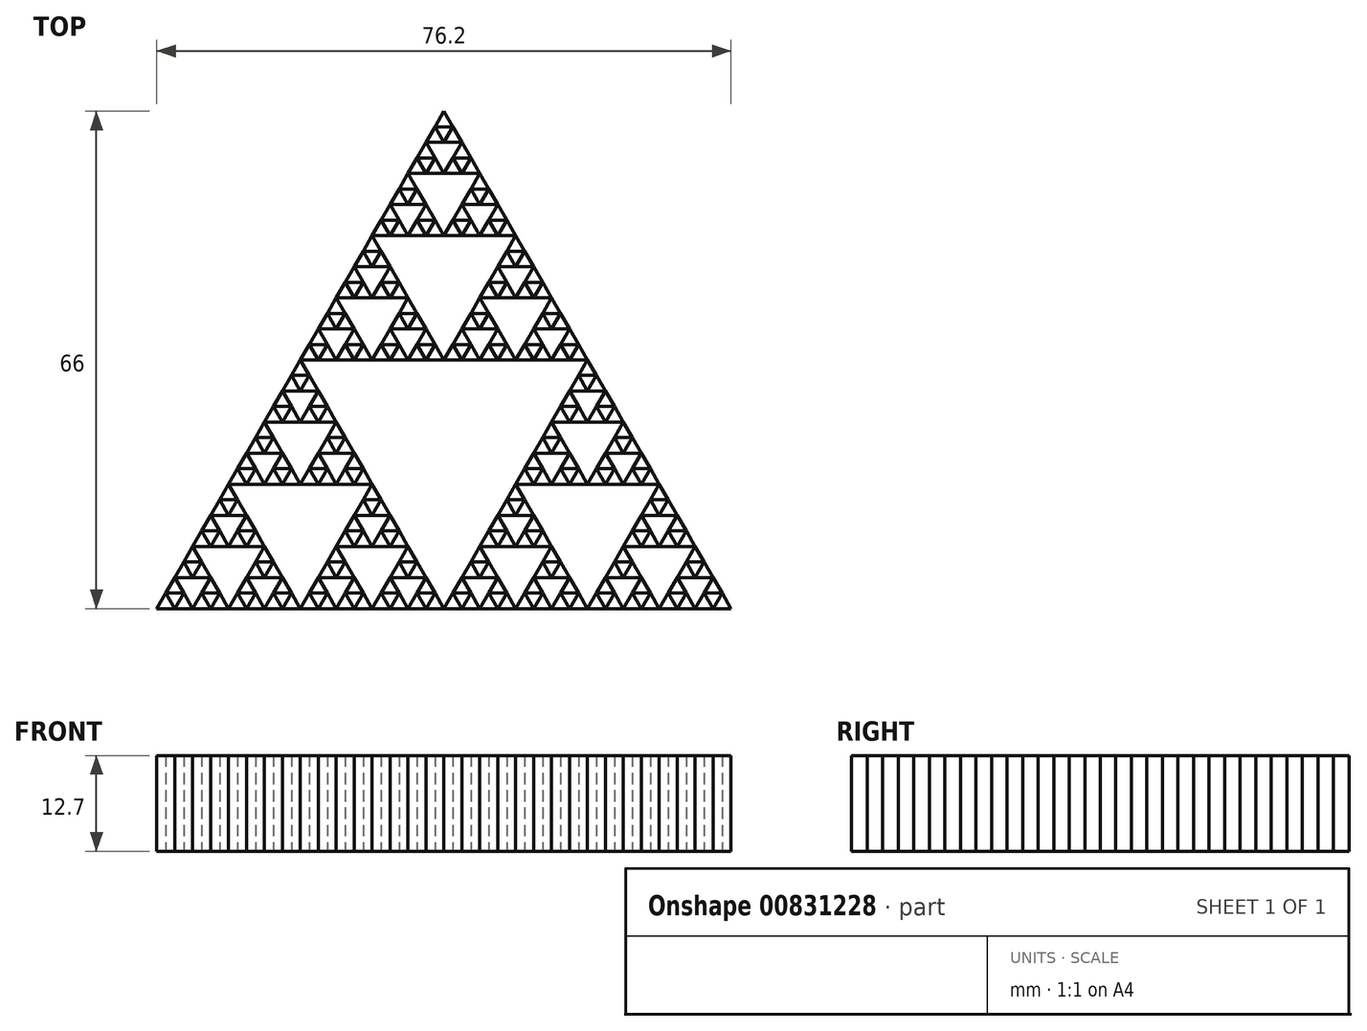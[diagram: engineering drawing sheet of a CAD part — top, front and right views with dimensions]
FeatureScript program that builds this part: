
annotation { "Feature Type Name" : "Feature", "Feature Type Description" : "" }
export const myFeature = defineFeature(function(context is Context, id is Id, definition is map)
    precondition{}
    {
        {
            var Q0;
            Q0=qCreatedBy(makeId("Top.planeOp"),FACE);
            var sketch = newSketch(context, id + "F0", { "sketchPlane" : qUnion([Q0])});
            skLineSegment(sketch, "E0", {"start": v(262.33, 166.64) * mm, "end": v(224.23, 100.64) * mm});
            skLineSegment(sketch, "E1", {"start": v(243.28, 133.64) * mm, "end": v(262.33, 100.64) * mm});
            skLineSegment(sketch, "E2", {"start": v(262.33, 100.64) * mm, "end": v(281.38, 133.64) * mm});
            skLineSegment(sketch, "E3", {"start": v(281.38, 133.64) * mm, "end": v(243.28, 133.64) * mm});
            skLineSegment(sketch, "E4", {"start": v(243.28, 133.64) * mm, "end": v(224.23, 100.64) * mm});
            skLineSegment(sketch, "E5", {"start": v(233.75, 117.14) * mm, "end": v(243.28, 100.64) * mm});
            skLineSegment(sketch, "E6", {"start": v(243.28, 100.64) * mm, "end": v(252.8, 117.14) * mm});
            skLineSegment(sketch, "E7", {"start": v(233.75, 117.14) * mm, "end": v(252.8, 117.14) * mm});
            skLineSegment(sketch, "E8", {"start": v(252.8, 150.14) * mm, "end": v(262.33, 133.64) * mm});
            skLineSegment(sketch, "E9", {"start": v(262.33, 133.64) * mm, "end": v(271.85, 150.14) * mm});
            skLineSegment(sketch, "E10", {"start": v(271.85, 150.14) * mm, "end": v(252.8, 150.14) * mm});
            skLineSegment(sketch, "E11", {"start": v(243.28, 117.14) * mm, "end": v(238.51, 125.4) * mm});
            skLineSegment(sketch, "E12", {"start": v(238.51, 125.4) * mm, "end": v(248.04, 125.4) * mm});
            skLineSegment(sketch, "E13", {"start": v(248.04, 125.4) * mm, "end": v(243.28, 117.14) * mm});
            skLineSegment(sketch, "E14", {"start": v(233.75, 100.64) * mm, "end": v(238.51, 108.9) * mm});
            skLineSegment(sketch, "E15", {"start": v(238.51, 108.9) * mm, "end": v(228.99, 108.9) * mm});
            skLineSegment(sketch, "E16", {"start": v(228.99, 108.9) * mm, "end": v(233.75, 100.64) * mm});
            skLineSegment(sketch, "E17", {"start": v(248.04, 108.9) * mm, "end": v(257.56, 108.9) * mm});
            skLineSegment(sketch, "E18", {"start": v(257.56, 108.9) * mm, "end": v(252.8, 100.64) * mm});
            skLineSegment(sketch, "E19", {"start": v(252.8, 100.64) * mm, "end": v(248.04, 108.9) * mm});
            skLineSegment(sketch, "E20", {"start": v(271.85, 117.14) * mm, "end": v(281.38, 100.64) * mm});
            skLineSegment(sketch, "E21", {"start": v(281.38, 100.64) * mm, "end": v(290.9, 117.14) * mm});
            skLineSegment(sketch, "E22", {"start": v(290.9, 117.14) * mm, "end": v(271.85, 117.14) * mm});
            skLineSegment(sketch, "E23", {"start": v(276.61, 108.9) * mm, "end": v(267.09, 108.9) * mm});
            skLineSegment(sketch, "E24", {"start": v(267.09, 108.9) * mm, "end": v(271.85, 100.64) * mm});
            skLineSegment(sketch, "E25", {"start": v(271.85, 100.64) * mm, "end": v(276.61, 108.9) * mm});
            skLineSegment(sketch, "E26", {"start": v(286.14, 108.9) * mm, "end": v(295.66, 108.9) * mm});
            skLineSegment(sketch, "E27", {"start": v(295.66, 108.9) * mm, "end": v(290.9, 100.64) * mm});
            skLineSegment(sketch, "E28", {"start": v(290.9, 100.64) * mm, "end": v(286.14, 108.9) * mm});
            skLineSegment(sketch, "E29", {"start": v(281.38, 117.14) * mm, "end": v(286.14, 125.4) * mm});
            skLineSegment(sketch, "E30", {"start": v(286.14, 125.4) * mm, "end": v(276.61, 125.4) * mm});
            skLineSegment(sketch, "E31", {"start": v(276.61, 125.4) * mm, "end": v(281.38, 117.14) * mm});
            skLineSegment(sketch, "E32", {"start": v(248.04, 141.89) * mm, "end": v(252.8, 133.64) * mm});
            skPoint(sketch, "E32.startSnap0", {"position": v(267.09, 141.89) * mm});
            skLineSegment(sketch, "E33", {"start": v(252.8, 133.64) * mm, "end": v(257.56, 141.89) * mm});
            skLineSegment(sketch, "E34", {"start": v(257.56, 141.89) * mm, "end": v(248.04, 141.89) * mm});
            skLineSegment(sketch, "E35", {"start": v(267.09, 141.89) * mm, "end": v(276.61, 141.89) * mm});
            skLineSegment(sketch, "E36", {"start": v(276.61, 141.89) * mm, "end": v(271.85, 133.64) * mm});
            skLineSegment(sketch, "E37", {"start": v(271.85, 133.64) * mm, "end": v(267.09, 141.89) * mm});
            skLineSegment(sketch, "E38", {"start": v(262.33, 150.14) * mm, "end": v(257.56, 158.39) * mm});
            skLineSegment(sketch, "E39", {"start": v(257.56, 158.39) * mm, "end": v(267.09, 158.39) * mm});
            skLineSegment(sketch, "E40", {"start": v(267.09, 158.39) * mm, "end": v(262.33, 150.14) * mm});
            skLineSegment(sketch, "E41", {"start": v(238.51, 117.14) * mm, "end": v(240.9, 121.27) * mm});
            skLineSegment(sketch, "E42", {"start": v(240.9, 121.27) * mm, "end": v(236.13, 121.27) * mm});
            skLineSegment(sketch, "E43", {"start": v(236.13, 121.27) * mm, "end": v(238.51, 117.14) * mm});
            skLineSegment(sketch, "E44", {"start": v(245.66, 121.27) * mm, "end": v(250.42, 121.27) * mm});
            skLineSegment(sketch, "E45", {"start": v(250.42, 121.27) * mm, "end": v(248.04, 117.14) * mm});
            skLineSegment(sketch, "E46", {"start": v(248.04, 117.14) * mm, "end": v(245.66, 121.27) * mm});
            skLineSegment(sketch, "E47", {"start": v(243.28, 125.4) * mm, "end": v(245.66, 129.52) * mm});
            skLineSegment(sketch, "E48", {"start": v(245.66, 129.52) * mm, "end": v(240.9, 129.52) * mm});
            skLineSegment(sketch, "E49", {"start": v(240.9, 129.52) * mm, "end": v(243.28, 125.4) * mm});
            skLineSegment(sketch, "E50", {"start": v(233.75, 108.9) * mm, "end": v(236.13, 113.02) * mm});
            skLineSegment(sketch, "E51", {"start": v(236.13, 113.02) * mm, "end": v(231.37, 113.02) * mm});
            skLineSegment(sketch, "E52", {"start": v(231.37, 113.02) * mm, "end": v(233.75, 108.9) * mm});
            skLineSegment(sketch, "E53", {"start": v(228.99, 100.64) * mm, "end": v(231.37, 104.77) * mm});
            skLineSegment(sketch, "E54", {"start": v(231.37, 104.77) * mm, "end": v(226.6, 104.77) * mm});
            skLineSegment(sketch, "E55", {"start": v(226.6, 104.77) * mm, "end": v(228.99, 100.64) * mm});
            skLineSegment(sketch, "E56", {"start": v(236.13, 104.77) * mm, "end": v(238.51, 100.64) * mm});
            skLineSegment(sketch, "E57", {"start": v(238.51, 100.64) * mm, "end": v(240.9, 104.77) * mm});
            skLineSegment(sketch, "E58", {"start": v(240.9, 104.77) * mm, "end": v(236.13, 104.77) * mm});
            skLineSegment(sketch, "E59", {"start": v(245.66, 104.77) * mm, "end": v(248.04, 100.64) * mm});
            skLineSegment(sketch, "E60", {"start": v(248.04, 100.64) * mm, "end": v(250.42, 104.77) * mm});
            skLineSegment(sketch, "E61", {"start": v(250.42, 104.77) * mm, "end": v(245.66, 104.77) * mm});
            skLineSegment(sketch, "E62", {"start": v(255.18, 104.77) * mm, "end": v(259.95, 104.77) * mm});
            skLineSegment(sketch, "E63", {"start": v(259.95, 104.77) * mm, "end": v(257.56, 100.64) * mm});
            skLineSegment(sketch, "E64", {"start": v(255.18, 104.77) * mm, "end": v(257.56, 100.64) * mm});
            skLineSegment(sketch, "E65", {"start": v(252.8, 108.9) * mm, "end": v(255.18, 113.02) * mm});
            skLineSegment(sketch, "E66", {"start": v(255.18, 113.02) * mm, "end": v(250.42, 113.02) * mm});
            skLineSegment(sketch, "E67", {"start": v(250.42, 113.02) * mm, "end": v(252.8, 108.9) * mm});
            skLineSegment(sketch, "E68", {"start": v(240.9, 100.64) * mm, "end": v(242.09, 102.7) * mm});
            skLineSegment(sketch, "E69", {"start": v(242.09, 102.7) * mm, "end": v(239.7, 102.7) * mm});
            skLineSegment(sketch, "E70", {"start": v(239.7, 102.7) * mm, "end": v(240.9, 100.64) * mm});
            skLineSegment(sketch, "E71", {"start": v(238.51, 100.64) * mm, "end": v(233.75, 100.64) * mm});
            skLineSegment(sketch, "E72", {"start": v(236.13, 100.64) * mm, "end": v(237.32, 102.7) * mm});
            skLineSegment(sketch, "E73", {"start": v(237.32, 102.7) * mm, "end": v(234.94, 102.7) * mm});
            skLineSegment(sketch, "E74", {"start": v(234.94, 102.7) * mm, "end": v(236.13, 100.64) * mm});
            skLineSegment(sketch, "E75", {"start": v(228.99, 100.64) * mm, "end": v(233.75, 100.64) * mm});
            skLineSegment(sketch, "E76", {"start": v(231.37, 100.64) * mm, "end": v(232.56, 102.7) * mm});
            skLineSegment(sketch, "E77", {"start": v(232.56, 102.7) * mm, "end": v(230.18, 102.7) * mm});
            skLineSegment(sketch, "E78", {"start": v(230.18, 102.7) * mm, "end": v(231.37, 100.64) * mm});
            skLineSegment(sketch, "E79", {"start": v(227.8, 102.7) * mm, "end": v(226.6, 100.64) * mm});
            skLineSegment(sketch, "E80", {"start": v(226.6, 100.64) * mm, "end": v(225.42, 102.7) * mm});
            skLineSegment(sketch, "E81", {"start": v(225.42, 102.7) * mm, "end": v(227.8, 102.7) * mm});
            skLineSegment(sketch, "E82", {"start": v(228.99, 104.77) * mm, "end": v(227.8, 106.83) * mm});
            skLineSegment(sketch, "E83", {"start": v(227.8, 106.83) * mm, "end": v(230.18, 106.83) * mm});
            skLineSegment(sketch, "E84", {"start": v(230.18, 106.83) * mm, "end": v(228.99, 104.77) * mm});
            skLineSegment(sketch, "E85", {"start": v(238.51, 104.77) * mm, "end": v(239.7, 106.83) * mm});
            skLineSegment(sketch, "E86", {"start": v(239.7, 106.83) * mm, "end": v(237.32, 106.83) * mm});
            skLineSegment(sketch, "E87", {"start": v(237.32, 106.83) * mm, "end": v(238.51, 104.77) * mm});
            skLineSegment(sketch, "E88", {"start": v(234.94, 110.96) * mm, "end": v(237.32, 110.96) * mm});
            skLineSegment(sketch, "E89", {"start": v(237.32, 110.96) * mm, "end": v(236.13, 108.9) * mm});
            skLineSegment(sketch, "E90", {"start": v(236.13, 108.9) * mm, "end": v(234.94, 110.96) * mm});
            skLineSegment(sketch, "E91", {"start": v(232.56, 110.96) * mm, "end": v(230.18, 110.96) * mm});
            skLineSegment(sketch, "E92", {"start": v(230.18, 110.96) * mm, "end": v(231.37, 108.9) * mm});
            skLineSegment(sketch, "E93", {"start": v(231.37, 108.9) * mm, "end": v(232.56, 110.96) * mm});
            skLineSegment(sketch, "E94", {"start": v(233.75, 117.14) * mm, "end": v(231.37, 113.02) * mm});
            skLineSegment(sketch, "E95", {"start": v(232.56, 115.08) * mm, "end": v(233.75, 113.02) * mm});
            skLineSegment(sketch, "E96", {"start": v(233.75, 113.02) * mm, "end": v(234.94, 115.08) * mm});
            skLineSegment(sketch, "E97", {"start": v(234.94, 115.08) * mm, "end": v(232.56, 115.08) * mm});
            skLineSegment(sketch, "E98", {"start": v(246.85, 102.7) * mm, "end": v(244.47, 102.7) * mm});
            skLineSegment(sketch, "E99", {"start": v(244.47, 102.7) * mm, "end": v(245.66, 100.64) * mm});
            skLineSegment(sketch, "E100", {"start": v(245.66, 100.64) * mm, "end": v(246.85, 102.7) * mm});
            skLineSegment(sketch, "E101", {"start": v(249.23, 102.7) * mm, "end": v(251.61, 102.7) * mm});
            skLineSegment(sketch, "E102", {"start": v(251.61, 102.7) * mm, "end": v(250.42, 100.64) * mm});
            skLineSegment(sketch, "E103", {"start": v(250.42, 100.64) * mm, "end": v(249.23, 102.7) * mm});
            skLineSegment(sketch, "E104", {"start": v(248.04, 104.77) * mm, "end": v(249.23, 106.83) * mm});
            skLineSegment(sketch, "E105", {"start": v(249.23, 106.83) * mm, "end": v(246.85, 106.83) * mm});
            skLineSegment(sketch, "E106", {"start": v(246.85, 106.83) * mm, "end": v(248.04, 104.77) * mm});
            skLineSegment(sketch, "E107", {"start": v(257.56, 104.77) * mm, "end": v(258.76, 106.83) * mm});
            skLineSegment(sketch, "E108", {"start": v(258.76, 106.83) * mm, "end": v(256.37, 106.83) * mm});
            skLineSegment(sketch, "E109", {"start": v(256.37, 106.83) * mm, "end": v(257.56, 104.77) * mm});
            skLineSegment(sketch, "E110", {"start": v(256.37, 102.7) * mm, "end": v(254, 102.7) * mm});
            skLineSegment(sketch, "E111", {"start": v(254, 102.7) * mm, "end": v(255.18, 100.64) * mm});
            skLineSegment(sketch, "E112", {"start": v(255.18, 100.64) * mm, "end": v(256.37, 102.7) * mm});
            skLineSegment(sketch, "E113", {"start": v(258.76, 102.7) * mm, "end": v(259.95, 100.64) * mm});
            skLineSegment(sketch, "E114", {"start": v(259.95, 100.64) * mm, "end": v(261.14, 102.7) * mm});
            skLineSegment(sketch, "E115", {"start": v(261.14, 102.7) * mm, "end": v(258.76, 102.7) * mm});
            skLineSegment(sketch, "E116", {"start": v(251.61, 110.96) * mm, "end": v(250.42, 108.9) * mm});
            skLineSegment(sketch, "E117", {"start": v(250.42, 108.9) * mm, "end": v(249.23, 110.96) * mm});
            skLineSegment(sketch, "E118", {"start": v(249.23, 110.96) * mm, "end": v(251.61, 110.96) * mm});
            skLineSegment(sketch, "E119", {"start": v(254, 110.96) * mm, "end": v(256.37, 110.96) * mm});
            skLineSegment(sketch, "E120", {"start": v(256.37, 110.96) * mm, "end": v(255.18, 108.9) * mm});
            skLineSegment(sketch, "E121", {"start": v(255.18, 108.9) * mm, "end": v(254, 110.96) * mm});
            skLineSegment(sketch, "E122", {"start": v(252.8, 113.02) * mm, "end": v(254, 115.08) * mm});
            skLineSegment(sketch, "E123", {"start": v(254, 115.08) * mm, "end": v(251.61, 115.08) * mm});
            skLineSegment(sketch, "E124", {"start": v(251.61, 115.08) * mm, "end": v(252.8, 113.02) * mm});
            skLineSegment(sketch, "E125", {"start": v(239.7, 119.2) * mm, "end": v(242.09, 119.2) * mm});
            skLineSegment(sketch, "E126", {"start": v(242.09, 119.2) * mm, "end": v(240.9, 117.14) * mm});
            skLineSegment(sketch, "E127", {"start": v(240.9, 117.14) * mm, "end": v(239.7, 119.2) * mm});
            skLineSegment(sketch, "E128", {"start": v(237.32, 119.2) * mm, "end": v(234.94, 119.2) * mm});
            skLineSegment(sketch, "E129", {"start": v(234.94, 119.2) * mm, "end": v(236.13, 117.14) * mm});
            skLineSegment(sketch, "E130", {"start": v(236.13, 117.14) * mm, "end": v(237.32, 119.2) * mm});
            skLineSegment(sketch, "E131", {"start": v(238.51, 121.27) * mm, "end": v(237.32, 123.33) * mm});
            skLineSegment(sketch, "E132", {"start": v(237.32, 123.33) * mm, "end": v(239.7, 123.33) * mm});
            skLineSegment(sketch, "E133", {"start": v(239.7, 123.33) * mm, "end": v(238.51, 121.27) * mm});
            skLineSegment(sketch, "E134", {"start": v(242.09, 127.45) * mm, "end": v(240.9, 125.4) * mm});
            skLineSegment(sketch, "E135", {"start": v(240.9, 125.4) * mm, "end": v(239.7, 127.45) * mm});
            skLineSegment(sketch, "E136", {"start": v(239.7, 127.45) * mm, "end": v(242.09, 127.45) * mm});
            skLineSegment(sketch, "E137", {"start": v(244.47, 127.45) * mm, "end": v(246.85, 127.45) * mm});
            skLineSegment(sketch, "E138", {"start": v(246.85, 127.45) * mm, "end": v(245.66, 125.4) * mm});
            skLineSegment(sketch, "E139", {"start": v(245.66, 125.4) * mm, "end": v(244.47, 127.45) * mm});
            skLineSegment(sketch, "E140", {"start": v(243.28, 129.52) * mm, "end": v(244.47, 131.58) * mm});
            skLineSegment(sketch, "E141", {"start": v(244.47, 131.58) * mm, "end": v(242.09, 131.58) * mm});
            skLineSegment(sketch, "E142", {"start": v(242.09, 131.58) * mm, "end": v(243.28, 129.52) * mm});
            skLineSegment(sketch, "E143", {"start": v(246.85, 119.2) * mm, "end": v(244.47, 119.2) * mm});
            skLineSegment(sketch, "E144", {"start": v(244.47, 119.2) * mm, "end": v(245.66, 117.14) * mm});
            skLineSegment(sketch, "E145", {"start": v(245.66, 117.14) * mm, "end": v(246.85, 119.2) * mm});
            skLineSegment(sketch, "E146", {"start": v(246.85, 123.33) * mm, "end": v(249.23, 123.33) * mm});
            skLineSegment(sketch, "E147", {"start": v(249.23, 123.33) * mm, "end": v(248.04, 121.27) * mm});
            skLineSegment(sketch, "E148", {"start": v(248.04, 121.27) * mm, "end": v(246.85, 123.33) * mm});
            skLineSegment(sketch, "E149", {"start": v(249.23, 119.2) * mm, "end": v(251.61, 119.2) * mm});
            skLineSegment(sketch, "E150", {"start": v(251.61, 119.2) * mm, "end": v(250.42, 117.14) * mm});
            skLineSegment(sketch, "E151", {"start": v(250.42, 117.14) * mm, "end": v(249.23, 119.2) * mm});
            skLineSegment(sketch, "E152.MirrorCS", {"start": v(298.05, 100.64) * mm, "end": v(299.24, 102.7) * mm});
            skLineSegment(sketch, "E153.MirrorCS", {"start": v(299.24, 102.7) * mm, "end": v(296.86, 102.7) * mm});
            skLineSegment(sketch, "E154.MirrorCS", {"start": v(296.86, 102.7) * mm, "end": v(298.05, 100.64) * mm});
            skLineSegment(sketch, "E155.MirrorCS", {"start": v(298.05, 104.77) * mm, "end": v(295.66, 100.64) * mm});
            skLineSegment(sketch, "E156.MirrorCS", {"start": v(295.66, 100.64) * mm, "end": v(293.28, 104.77) * mm});
            skLineSegment(sketch, "E157.MirrorCS", {"start": v(289.71, 102.7) * mm, "end": v(288.52, 100.64) * mm});
            skLineSegment(sketch, "E158.MirrorCS", {"start": v(288.52, 100.64) * mm, "end": v(287.33, 102.7) * mm});
            skLineSegment(sketch, "E159.MirrorCS", {"start": v(287.33, 102.7) * mm, "end": v(289.71, 102.7) * mm});
            skLineSegment(sketch, "E160.MirrorCS", {"start": v(293.28, 104.77) * mm, "end": v(298.05, 104.77) * mm});
            skLineSegment(sketch, "E161.MirrorCS", {"start": v(294.47, 106.83) * mm, "end": v(295.66, 104.77) * mm});
            skLineSegment(sketch, "E162.MirrorCS", {"start": v(295.66, 104.77) * mm, "end": v(296.86, 106.83) * mm});
            skLineSegment(sketch, "E163.MirrorCS", {"start": v(296.86, 106.83) * mm, "end": v(294.47, 106.83) * mm});
            skLineSegment(sketch, "E164.MirrorCS", {"start": v(293.28, 100.64) * mm, "end": v(292.1, 102.7) * mm});
            skLineSegment(sketch, "E165.MirrorCS", {"start": v(292.1, 102.7) * mm, "end": v(294.47, 102.7) * mm});
            skLineSegment(sketch, "E166.MirrorCS", {"start": v(294.47, 102.7) * mm, "end": v(293.28, 100.64) * mm});
            skLineSegment(sketch, "E167.MirrorCS", {"start": v(284.95, 102.7) * mm, "end": v(283.76, 100.64) * mm});
            skLineSegment(sketch, "E168.MirrorCS", {"start": v(283.76, 100.64) * mm, "end": v(282.57, 102.7) * mm});
            skLineSegment(sketch, "E169.MirrorCS", {"start": v(282.57, 102.7) * mm, "end": v(284.95, 102.7) * mm});
            skLineSegment(sketch, "E170.MirrorCS", {"start": v(286.14, 104.77) * mm, "end": v(284.95, 106.83) * mm});
            skLineSegment(sketch, "E171.MirrorCS", {"start": v(287.33, 106.83) * mm, "end": v(286.14, 104.77) * mm});
            skLineSegment(sketch, "E172.MirrorCS", {"start": v(284.95, 106.83) * mm, "end": v(287.33, 106.83) * mm});
            skLineSegment(sketch, "E173.MirrorCS", {"start": v(286.14, 100.64) * mm, "end": v(283.76, 104.77) * mm});
            skLineSegment(sketch, "E174.MirrorCS", {"start": v(288.52, 104.77) * mm, "end": v(286.14, 100.64) * mm});
            skLineSegment(sketch, "E175.MirrorCS", {"start": v(283.76, 104.77) * mm, "end": v(288.52, 104.77) * mm});
            skLineSegment(sketch, "E176.MirrorCS", {"start": v(287.33, 110.96) * mm, "end": v(288.52, 108.9) * mm});
            skLineSegment(sketch, "E177.MirrorCS", {"start": v(288.52, 108.9) * mm, "end": v(289.71, 110.96) * mm});
            skLineSegment(sketch, "E178.MirrorCS", {"start": v(289.71, 110.96) * mm, "end": v(287.33, 110.96) * mm});
            skLineSegment(sketch, "E179.MirrorCS", {"start": v(290.9, 108.9) * mm, "end": v(288.52, 113.02) * mm});
            skLineSegment(sketch, "E180.MirrorCS", {"start": v(288.52, 113.02) * mm, "end": v(293.28, 113.02) * mm});
            skLineSegment(sketch, "E181.MirrorCS", {"start": v(290.9, 113.02) * mm, "end": v(289.71, 115.08) * mm});
            skLineSegment(sketch, "E182.MirrorCS", {"start": v(292.1, 115.08) * mm, "end": v(290.9, 113.02) * mm});
            skLineSegment(sketch, "E183.MirrorCS", {"start": v(289.71, 115.08) * mm, "end": v(292.1, 115.08) * mm});
            skLineSegment(sketch, "E184.MirrorCS", {"start": v(293.28, 113.02) * mm, "end": v(290.9, 108.9) * mm});
            skLineSegment(sketch, "E185.MirrorCS", {"start": v(292.1, 110.96) * mm, "end": v(294.47, 110.96) * mm});
            skLineSegment(sketch, "E186.MirrorCS", {"start": v(293.28, 108.9) * mm, "end": v(292.1, 110.96) * mm});
            skLineSegment(sketch, "E187.MirrorCS", {"start": v(294.47, 110.96) * mm, "end": v(293.28, 108.9) * mm});
            skLineSegment(sketch, "E188.MirrorCS", {"start": v(288.52, 117.14) * mm, "end": v(287.33, 119.2) * mm});
            skLineSegment(sketch, "E189.MirrorCS", {"start": v(289.71, 119.2) * mm, "end": v(288.52, 117.14) * mm});
            skLineSegment(sketch, "E190.MirrorCS", {"start": v(287.33, 119.2) * mm, "end": v(289.71, 119.2) * mm});
            skLineSegment(sketch, "E191.MirrorCS", {"start": v(288.52, 121.27) * mm, "end": v(286.14, 117.14) * mm});
            skLineSegment(sketch, "E192.MirrorCS", {"start": v(286.14, 117.14) * mm, "end": v(283.76, 121.27) * mm});
            skLineSegment(sketch, "E193.MirrorCS", {"start": v(284.95, 119.2) * mm, "end": v(282.57, 119.2) * mm});
            skLineSegment(sketch, "E194.MirrorCS", {"start": v(283.76, 117.14) * mm, "end": v(284.95, 119.2) * mm});
            skLineSegment(sketch, "E195.MirrorCS", {"start": v(282.57, 119.2) * mm, "end": v(283.76, 117.14) * mm});
            skLineSegment(sketch, "E196.MirrorCS", {"start": v(283.76, 121.27) * mm, "end": v(288.52, 121.27) * mm});
            skLineSegment(sketch, "E197.MirrorCS", {"start": v(284.95, 123.33) * mm, "end": v(286.14, 121.27) * mm});
            skLineSegment(sketch, "E198.MirrorCS", {"start": v(286.14, 121.27) * mm, "end": v(287.33, 123.33) * mm});
            skLineSegment(sketch, "E199.MirrorCS", {"start": v(287.33, 123.33) * mm, "end": v(284.95, 123.33) * mm});
            skLineSegment(sketch, "E200.MirrorCS", {"start": v(274.23, 117.14) * mm, "end": v(275.42, 119.2) * mm});
            skLineSegment(sketch, "E201.MirrorCS", {"start": v(275.42, 119.2) * mm, "end": v(273.04, 119.2) * mm});
            skLineSegment(sketch, "E202.MirrorCS", {"start": v(273.04, 119.2) * mm, "end": v(274.23, 117.14) * mm});
            skLineSegment(sketch, "E203.MirrorCS", {"start": v(279, 117.14) * mm, "end": v(277.8, 119.2) * mm});
            skLineSegment(sketch, "E204.MirrorCS", {"start": v(280.19, 119.2) * mm, "end": v(279, 117.14) * mm});
            skLineSegment(sketch, "E205.MirrorCS", {"start": v(277.8, 119.2) * mm, "end": v(280.19, 119.2) * mm});
            skLineSegment(sketch, "E206.MirrorCS", {"start": v(279, 121.27) * mm, "end": v(274.23, 121.27) * mm});
            skLineSegment(sketch, "E207.MirrorCS", {"start": v(276.61, 117.14) * mm, "end": v(279, 121.27) * mm});
            skLineSegment(sketch, "E208.MirrorCS", {"start": v(274.23, 121.27) * mm, "end": v(276.61, 117.14) * mm});
            skLineSegment(sketch, "E209.MirrorCS", {"start": v(275.42, 123.33) * mm, "end": v(276.61, 121.27) * mm});
            skLineSegment(sketch, "E210.MirrorCS", {"start": v(277.8, 123.33) * mm, "end": v(275.42, 123.33) * mm});
            skLineSegment(sketch, "E211.MirrorCS", {"start": v(276.61, 121.27) * mm, "end": v(277.8, 123.33) * mm});
            skLineSegment(sketch, "E212.MirrorCS", {"start": v(277.8, 127.45) * mm, "end": v(279, 125.4) * mm});
            skLineSegment(sketch, "E213.MirrorCS", {"start": v(279, 125.4) * mm, "end": v(280.19, 127.45) * mm});
            skLineSegment(sketch, "E214.MirrorCS", {"start": v(281.38, 125.4) * mm, "end": v(279, 129.52) * mm});
            skLineSegment(sketch, "E215.MirrorCS", {"start": v(283.76, 129.52) * mm, "end": v(281.38, 125.4) * mm});
            skLineSegment(sketch, "E216.MirrorCS", {"start": v(282.57, 127.45) * mm, "end": v(283.76, 125.4) * mm});
            skLineSegment(sketch, "E217.MirrorCS", {"start": v(283.76, 125.4) * mm, "end": v(284.95, 127.45) * mm});
            skLineSegment(sketch, "E218.MirrorCS", {"start": v(284.95, 127.45) * mm, "end": v(282.57, 127.45) * mm});
            skLineSegment(sketch, "E219.MirrorCS", {"start": v(280.19, 127.45) * mm, "end": v(277.8, 127.45) * mm});
            skLineSegment(sketch, "E220.MirrorCS", {"start": v(281.38, 129.52) * mm, "end": v(280.19, 131.58) * mm});
            skLineSegment(sketch, "E221.MirrorCS", {"start": v(282.57, 131.58) * mm, "end": v(281.38, 129.52) * mm});
            skLineSegment(sketch, "E222.MirrorCS", {"start": v(280.19, 131.58) * mm, "end": v(282.57, 131.58) * mm});
            skLineSegment(sketch, "E223.MirrorCS", {"start": v(279, 129.52) * mm, "end": v(283.76, 129.52) * mm});
            skLineSegment(sketch, "E224.MirrorCS", {"start": v(265.9, 102.7) * mm, "end": v(264.7, 100.64) * mm});
            skLineSegment(sketch, "E225.MirrorCS", {"start": v(264.7, 100.64) * mm, "end": v(263.52, 102.7) * mm});
            skLineSegment(sketch, "E226.MirrorCS", {"start": v(263.52, 102.7) * mm, "end": v(265.9, 102.7) * mm});
            skLineSegment(sketch, "E227.MirrorCS", {"start": v(264.7, 104.77) * mm, "end": v(267.09, 100.64) * mm});
            skLineSegment(sketch, "E228.MirrorCS", {"start": v(269.47, 104.77) * mm, "end": v(267.09, 100.64) * mm});
            skLineSegment(sketch, "E229.MirrorCS", {"start": v(269.47, 100.64) * mm, "end": v(268.28, 102.7) * mm});
            skLineSegment(sketch, "E230.MirrorCS", {"start": v(270.66, 102.7) * mm, "end": v(269.47, 100.64) * mm});
            skLineSegment(sketch, "E231.MirrorCS", {"start": v(268.28, 102.7) * mm, "end": v(270.66, 102.7) * mm});
            skLineSegment(sketch, "E232.MirrorCS", {"start": v(269.47, 104.77) * mm, "end": v(264.7, 104.77) * mm});
            skLineSegment(sketch, "E233.MirrorCS", {"start": v(268.28, 106.83) * mm, "end": v(267.09, 104.77) * mm});
            skLineSegment(sketch, "E234.MirrorCS", {"start": v(267.09, 104.77) * mm, "end": v(265.9, 106.83) * mm});
            skLineSegment(sketch, "E235.MirrorCS", {"start": v(265.9, 106.83) * mm, "end": v(268.28, 106.83) * mm});
            skLineSegment(sketch, "E236.MirrorCS", {"start": v(273.04, 102.7) * mm, "end": v(274.23, 100.64) * mm});
            skLineSegment(sketch, "E237.MirrorCS", {"start": v(274.23, 100.64) * mm, "end": v(275.42, 102.7) * mm});
            skLineSegment(sketch, "E238.MirrorCS", {"start": v(275.42, 102.7) * mm, "end": v(273.04, 102.7) * mm});
            skLineSegment(sketch, "E239.MirrorCS", {"start": v(276.61, 100.64) * mm, "end": v(274.23, 104.77) * mm});
            skLineSegment(sketch, "E240.MirrorCS", {"start": v(274.23, 104.77) * mm, "end": v(279, 104.77) * mm});
            skLineSegment(sketch, "E241.MirrorCS", {"start": v(276.61, 104.77) * mm, "end": v(275.42, 106.83) * mm});
            skLineSegment(sketch, "E242.MirrorCS", {"start": v(275.42, 106.83) * mm, "end": v(277.8, 106.83) * mm});
            skLineSegment(sketch, "E243.MirrorCS", {"start": v(277.8, 106.83) * mm, "end": v(276.61, 104.77) * mm});
            skLineSegment(sketch, "E244.MirrorCS", {"start": v(279, 104.77) * mm, "end": v(276.61, 100.64) * mm});
            skLineSegment(sketch, "E245.MirrorCS", {"start": v(277.8, 102.7) * mm, "end": v(280.19, 102.7) * mm});
            skLineSegment(sketch, "E246.MirrorCS", {"start": v(279, 100.64) * mm, "end": v(277.8, 102.7) * mm});
            skLineSegment(sketch, "E247.MirrorCS", {"start": v(280.19, 102.7) * mm, "end": v(279, 100.64) * mm});
            skLineSegment(sketch, "E248.MirrorCS", {"start": v(273.04, 110.96) * mm, "end": v(274.23, 108.9) * mm});
            skLineSegment(sketch, "E249.MirrorCS", {"start": v(274.23, 108.9) * mm, "end": v(275.42, 110.96) * mm});
            skLineSegment(sketch, "E250.MirrorCS", {"start": v(275.42, 110.96) * mm, "end": v(273.04, 110.96) * mm});
            skLineSegment(sketch, "E251.MirrorCS", {"start": v(274.23, 113.02) * mm, "end": v(271.85, 108.9) * mm});
            skLineSegment(sketch, "E252.MirrorCS", {"start": v(271.85, 108.9) * mm, "end": v(269.47, 113.02) * mm});
            skLineSegment(sketch, "E253.MirrorCS", {"start": v(270.66, 110.96) * mm, "end": v(268.28, 110.96) * mm});
            skLineSegment(sketch, "E254.MirrorCS", {"start": v(269.47, 108.9) * mm, "end": v(270.66, 110.96) * mm});
            skLineSegment(sketch, "E255.MirrorCS", {"start": v(268.28, 110.96) * mm, "end": v(269.47, 108.9) * mm});
            skLineSegment(sketch, "E256.MirrorCS", {"start": v(271.85, 113.02) * mm, "end": v(270.66, 115.08) * mm});
            skLineSegment(sketch, "E257.MirrorCS", {"start": v(273.04, 115.08) * mm, "end": v(271.85, 113.02) * mm});
            skLineSegment(sketch, "E258.MirrorCS", {"start": v(270.66, 115.08) * mm, "end": v(273.04, 115.08) * mm});
            skLineSegment(sketch, "E259.MirrorCS", {"start": v(269.47, 113.02) * mm, "end": v(274.23, 113.02) * mm});
            skLineSegment(sketch, "E260", {"start": v(269.47, 137.76) * mm, "end": v(264.7, 137.76) * mm});
            skLineSegment(sketch, "E261", {"start": v(264.7, 137.76) * mm, "end": v(267.09, 133.64) * mm});
            skLineSegment(sketch, "E262", {"start": v(267.09, 133.64) * mm, "end": v(269.47, 137.76) * mm});
            skLineSegment(sketch, "E263", {"start": v(257.56, 141.89) * mm, "end": v(262.33, 133.64) * mm});
            skLineSegment(sketch, "E264", {"start": v(259.95, 137.76) * mm, "end": v(255.18, 137.76) * mm});
            skLineSegment(sketch, "E265", {"start": v(255.18, 137.76) * mm, "end": v(257.56, 133.64) * mm});
            skLineSegment(sketch, "E266", {"start": v(259.95, 137.76) * mm, "end": v(257.56, 133.64) * mm});
            skLineSegment(sketch, "E267", {"start": v(250.42, 137.76) * mm, "end": v(248.04, 133.64) * mm});
            skLineSegment(sketch, "E268", {"start": v(248.04, 133.64) * mm, "end": v(245.66, 137.76) * mm});
            skLineSegment(sketch, "E269", {"start": v(245.66, 137.76) * mm, "end": v(250.42, 137.76) * mm});
            skLineSegment(sketch, "E270", {"start": v(252.8, 141.89) * mm, "end": v(250.42, 146.01) * mm});
            skLineSegment(sketch, "E271", {"start": v(250.42, 146.01) * mm, "end": v(255.18, 146.01) * mm});
            skLineSegment(sketch, "E272", {"start": v(255.18, 146.01) * mm, "end": v(252.8, 141.89) * mm});
            skLineSegment(sketch, "E273", {"start": v(259.95, 154.26) * mm, "end": v(255.18, 154.26) * mm});
            skLineSegment(sketch, "E274", {"start": v(255.18, 154.26) * mm, "end": v(257.56, 150.14) * mm});
            skLineSegment(sketch, "E275", {"start": v(257.56, 150.14) * mm, "end": v(259.95, 154.26) * mm});
            skLineSegment(sketch, "E276", {"start": v(264.7, 154.26) * mm, "end": v(267.09, 150.14) * mm});
            skLineSegment(sketch, "E277", {"start": v(267.09, 150.14) * mm, "end": v(269.47, 154.26) * mm});
            skLineSegment(sketch, "E278", {"start": v(269.47, 154.26) * mm, "end": v(264.7, 154.26) * mm});
            skLineSegment(sketch, "E279", {"start": v(262.33, 158.39) * mm, "end": v(264.7, 162.51) * mm});
            skLineSegment(sketch, "E280", {"start": v(264.7, 162.51) * mm, "end": v(259.95, 162.51) * mm});
            skLineSegment(sketch, "E281", {"start": v(259.95, 162.51) * mm, "end": v(262.33, 158.39) * mm});
            skLineSegment(sketch, "E282", {"start": v(271.85, 141.89) * mm, "end": v(274.23, 146.01) * mm});
            skLineSegment(sketch, "E283", {"start": v(274.23, 146.01) * mm, "end": v(269.47, 146.01) * mm});
            skLineSegment(sketch, "E284", {"start": v(269.47, 146.01) * mm, "end": v(271.85, 141.89) * mm});
            skLineSegment(sketch, "E285", {"start": v(274.23, 137.76) * mm, "end": v(279, 137.76) * mm});
            skLineSegment(sketch, "E286", {"start": v(279, 137.76) * mm, "end": v(276.61, 133.64) * mm});
            skLineSegment(sketch, "E287", {"start": v(276.61, 133.64) * mm, "end": v(274.23, 137.76) * mm});
            skLineSegment(sketch, "E288", {"start": v(273.04, 143.95) * mm, "end": v(274.23, 141.89) * mm});
            skLineSegment(sketch, "E289", {"start": v(274.23, 141.89) * mm, "end": v(275.42, 143.95) * mm});
            skLineSegment(sketch, "E290", {"start": v(275.42, 143.95) * mm, "end": v(273.04, 143.95) * mm});
            skLineSegment(sketch, "E291", {"start": v(274.23, 133.64) * mm, "end": v(275.42, 135.7) * mm});
            skLineSegment(sketch, "E292", {"start": v(275.42, 135.7) * mm, "end": v(273.04, 135.7) * mm});
            skLineSegment(sketch, "E293", {"start": v(273.04, 135.7) * mm, "end": v(274.23, 133.64) * mm});
            skLineSegment(sketch, "E294", {"start": v(268.28, 135.7) * mm, "end": v(270.66, 135.7) * mm});
            skLineSegment(sketch, "E295", {"start": v(270.66, 135.7) * mm, "end": v(269.47, 133.64) * mm});
            skLineSegment(sketch, "E296", {"start": v(269.47, 133.64) * mm, "end": v(268.28, 135.7) * mm});
            skLineSegment(sketch, "E297", {"start": v(265.9, 135.7) * mm, "end": v(263.52, 135.7) * mm});
            skLineSegment(sketch, "E298", {"start": v(263.52, 135.7) * mm, "end": v(264.7, 133.64) * mm});
            skLineSegment(sketch, "E299", {"start": v(264.7, 133.64) * mm, "end": v(265.9, 135.7) * mm});
            skLineSegment(sketch, "E300", {"start": v(267.09, 137.76) * mm, "end": v(268.28, 139.83) * mm});
            skLineSegment(sketch, "E301", {"start": v(268.28, 139.83) * mm, "end": v(265.9, 139.83) * mm});
            skLineSegment(sketch, "E302", {"start": v(265.9, 139.83) * mm, "end": v(267.09, 137.76) * mm});
            skLineSegment(sketch, "E303", {"start": v(277.8, 135.7) * mm, "end": v(280.19, 135.7) * mm});
            skLineSegment(sketch, "E304", {"start": v(280.19, 135.7) * mm, "end": v(279, 133.64) * mm});
            skLineSegment(sketch, "E305", {"start": v(279, 133.64) * mm, "end": v(277.8, 135.7) * mm});
            skLineSegment(sketch, "E306", {"start": v(276.61, 137.76) * mm, "end": v(277.8, 139.83) * mm});
            skLineSegment(sketch, "E307", {"start": v(277.8, 139.83) * mm, "end": v(275.42, 139.83) * mm});
            skLineSegment(sketch, "E308", {"start": v(275.42, 139.83) * mm, "end": v(276.61, 137.76) * mm});
            skLineSegment(sketch, "E309", {"start": v(270.66, 143.95) * mm, "end": v(269.47, 141.89) * mm});
            skLineSegment(sketch, "E310", {"start": v(269.47, 141.89) * mm, "end": v(268.28, 143.95) * mm});
            skLineSegment(sketch, "E311", {"start": v(268.28, 143.95) * mm, "end": v(270.66, 143.95) * mm});
            skLineSegment(sketch, "E312", {"start": v(271.85, 146.01) * mm, "end": v(273.04, 148.08) * mm});
            skLineSegment(sketch, "E313", {"start": v(273.04, 148.08) * mm, "end": v(270.66, 148.08) * mm});
            skLineSegment(sketch, "E314", {"start": v(270.66, 148.08) * mm, "end": v(271.85, 146.01) * mm});
            skLineSegment(sketch, "E315", {"start": v(265.9, 152.2) * mm, "end": v(264.7, 150.14) * mm});
            skLineSegment(sketch, "E316", {"start": v(264.7, 150.14) * mm, "end": v(263.52, 152.2) * mm});
            skLineSegment(sketch, "E317", {"start": v(263.52, 152.2) * mm, "end": v(265.9, 152.2) * mm});
            skLineSegment(sketch, "E318", {"start": v(268.28, 152.2) * mm, "end": v(270.66, 152.2) * mm});
            skLineSegment(sketch, "E319", {"start": v(270.66, 152.2) * mm, "end": v(269.47, 150.14) * mm});
            skLineSegment(sketch, "E320", {"start": v(269.47, 150.14) * mm, "end": v(268.28, 152.2) * mm});
            skLineSegment(sketch, "E321", {"start": v(258.76, 135.7) * mm, "end": v(261.14, 135.7) * mm});
            skLineSegment(sketch, "E322", {"start": v(261.14, 135.7) * mm, "end": v(259.95, 133.64) * mm});
            skLineSegment(sketch, "E323", {"start": v(259.95, 133.64) * mm, "end": v(258.76, 135.7) * mm});
            skLineSegment(sketch, "E324", {"start": v(256.37, 135.7) * mm, "end": v(254, 135.7) * mm});
            skLineSegment(sketch, "E325", {"start": v(254, 135.7) * mm, "end": v(255.18, 133.64) * mm});
            skLineSegment(sketch, "E326", {"start": v(255.18, 133.64) * mm, "end": v(256.37, 135.7) * mm});
            skLineSegment(sketch, "E327", {"start": v(249.23, 135.7) * mm, "end": v(251.61, 135.7) * mm});
            skLineSegment(sketch, "E328", {"start": v(251.61, 135.7) * mm, "end": v(250.42, 133.64) * mm});
            skLineSegment(sketch, "E329", {"start": v(250.42, 133.64) * mm, "end": v(249.23, 135.7) * mm});
            skLineSegment(sketch, "E330", {"start": v(246.85, 135.7) * mm, "end": v(245.66, 133.64) * mm});
            skLineSegment(sketch, "E331", {"start": v(245.66, 133.64) * mm, "end": v(244.47, 135.7) * mm});
            skLineSegment(sketch, "E332", {"start": v(244.47, 135.7) * mm, "end": v(246.85, 135.7) * mm});
            skLineSegment(sketch, "E333", {"start": v(248.04, 137.76) * mm, "end": v(249.23, 139.83) * mm});
            skLineSegment(sketch, "E334", {"start": v(249.23, 139.83) * mm, "end": v(246.85, 139.83) * mm});
            skLineSegment(sketch, "E335", {"start": v(246.85, 139.83) * mm, "end": v(248.04, 137.76) * mm});
            skLineSegment(sketch, "E336", {"start": v(257.56, 137.76) * mm, "end": v(258.76, 139.83) * mm});
            skLineSegment(sketch, "E337", {"start": v(258.76, 139.83) * mm, "end": v(256.37, 139.83) * mm});
            skLineSegment(sketch, "E338", {"start": v(256.37, 139.83) * mm, "end": v(257.56, 137.76) * mm});
            skLineSegment(sketch, "E339", {"start": v(254, 143.95) * mm, "end": v(256.37, 143.95) * mm});
            skLineSegment(sketch, "E340", {"start": v(256.37, 143.95) * mm, "end": v(255.18, 141.89) * mm});
            skLineSegment(sketch, "E341", {"start": v(255.18, 141.89) * mm, "end": v(254, 143.95) * mm});
            skLineSegment(sketch, "E342", {"start": v(249.23, 143.95) * mm, "end": v(251.61, 143.95) * mm});
            skLineSegment(sketch, "E343", {"start": v(251.61, 143.95) * mm, "end": v(250.42, 141.89) * mm});
            skLineSegment(sketch, "E344", {"start": v(250.42, 141.89) * mm, "end": v(249.23, 143.95) * mm});
            skLineSegment(sketch, "E345", {"start": v(252.8, 146.01) * mm, "end": v(254, 148.08) * mm});
            skLineSegment(sketch, "E346", {"start": v(254, 148.08) * mm, "end": v(251.61, 148.08) * mm});
            skLineSegment(sketch, "E347", {"start": v(251.61, 148.08) * mm, "end": v(252.8, 146.01) * mm});
            skLineSegment(sketch, "E348", {"start": v(258.76, 152.2) * mm, "end": v(259.95, 150.14) * mm});
            skLineSegment(sketch, "E349", {"start": v(259.95, 150.14) * mm, "end": v(261.14, 152.2) * mm});
            skLineSegment(sketch, "E350", {"start": v(261.14, 152.2) * mm, "end": v(258.76, 152.2) * mm});
            skLineSegment(sketch, "E351", {"start": v(255.18, 150.14) * mm, "end": v(256.37, 152.2) * mm});
            skLineSegment(sketch, "E352", {"start": v(256.37, 152.2) * mm, "end": v(254, 152.2) * mm});
            skLineSegment(sketch, "E353", {"start": v(254, 152.2) * mm, "end": v(255.18, 150.14) * mm});
            skLineSegment(sketch, "E354", {"start": v(257.56, 154.26) * mm, "end": v(258.76, 156.32) * mm});
            skLineSegment(sketch, "E355", {"start": v(258.76, 156.32) * mm, "end": v(256.37, 156.32) * mm});
            skLineSegment(sketch, "E356", {"start": v(256.37, 156.32) * mm, "end": v(257.56, 154.26) * mm});
            skLineSegment(sketch, "E357", {"start": v(267.09, 154.26) * mm, "end": v(268.28, 156.32) * mm});
            skLineSegment(sketch, "E358", {"start": v(268.28, 156.32) * mm, "end": v(265.9, 156.32) * mm});
            skLineSegment(sketch, "E359", {"start": v(265.9, 156.32) * mm, "end": v(267.09, 154.26) * mm});
            skLineSegment(sketch, "E360", {"start": v(261.14, 160.45) * mm, "end": v(258.76, 160.45) * mm});
            skPoint(sketch, "E360.endSnap0", {"position": v(261.14, 160.45) * mm});
            skLineSegment(sketch, "E361", {"start": v(258.76, 160.45) * mm, "end": v(259.95, 158.39) * mm});
            skLineSegment(sketch, "E362", {"start": v(259.95, 158.39) * mm, "end": v(261.14, 160.45) * mm});
            skLineSegment(sketch, "E363", {"start": v(263.52, 160.45) * mm, "end": v(265.9, 160.45) * mm});
            skLineSegment(sketch, "E364", {"start": v(263.52, 160.45) * mm, "end": v(264.7, 158.39) * mm});
            skPoint(sketch, "E364.endSnap0", {"position": v(264.7, 160.45) * mm});
            skLineSegment(sketch, "E365", {"start": v(264.7, 158.39) * mm, "end": v(265.9, 160.45) * mm});
            skLineSegment(sketch, "E366", {"start": v(262.33, 162.51) * mm, "end": v(263.52, 164.57) * mm});
            skLineSegment(sketch, "E367", {"start": v(263.52, 164.57) * mm, "end": v(261.14, 164.57) * mm});
            skLineSegment(sketch, "E368", {"start": v(261.14, 164.57) * mm, "end": v(262.33, 162.51) * mm});
            skLineSegment(sketch, "E369", {"start": v(300.43, 100.64) * mm, "end": v(262.33, 166.64) * mm});
            skLineSegment(sketch, "E370", {"start": v(224.23, 100.64) * mm, "end": v(300.43, 100.64) * mm});
            skSolve(sketch);
        }
        {
            var Q0;
            {var subQ3=sQuery(id+"F0.wireOp",EDGE,"E111");Q0=makeQuery(id+"F0.imprint","IMPRINT",FACE,{"disambiguationData":[TD([[makeQuery(id+"F0.imprint","IMPRINT",EDGE,{"derivedFrom":subQ3}),-1.0]])]});}
            var Q1;
            {var subQ3=sQuery(id+"F0.wireOp",EDGE,"E112");Q1=makeQuery(id+"F0.imprint","IMPRINT",FACE,{"disambiguationData":[TD([[makeQuery(id+"F0.imprint","IMPRINT",EDGE,{"derivedFrom":subQ3}),-1.0]])]});}
            var Q2;
            {var subQ3=sQuery(id+"F0.wireOp",EDGE,"E110");Q2=makeQuery(id+"F0.imprint","IMPRINT",FACE,{"disambiguationData":[TD([[makeQuery(id+"F0.imprint","IMPRINT",EDGE,{"derivedFrom":subQ3}),-1.0]])]});}
            var Q3;
            {var subQ3=sQuery(id+"F0.wireOp",EDGE,"E109");Q3=makeQuery(id+"F0.imprint","IMPRINT",FACE,{"disambiguationData":[TD([[makeQuery(id+"F0.imprint","IMPRINT",EDGE,{"derivedFrom":subQ3}),-1.0]])]});}
            var Q4;
            {var subQ3=sQuery(id+"F0.wireOp",EDGE,"E107");Q4=makeQuery(id+"F0.imprint","IMPRINT",FACE,{"disambiguationData":[TD([[makeQuery(id+"F0.imprint","IMPRINT",EDGE,{"derivedFrom":subQ3}),-1.0]])]});}
            var Q5;
            {var subQ3=sQuery(id+"F0.wireOp",EDGE,"E108");Q5=makeQuery(id+"F0.imprint","IMPRINT",FACE,{"disambiguationData":[TD([[makeQuery(id+"F0.imprint","IMPRINT",EDGE,{"derivedFrom":subQ3}),-1.0]])]});}
            var Q6;
            {var subQ3=sQuery(id+"F0.wireOp",EDGE,"E113");Q6=makeQuery(id+"F0.imprint","IMPRINT",FACE,{"disambiguationData":[TD([[makeQuery(id+"F0.imprint","IMPRINT",EDGE,{"derivedFrom":subQ3}),-1.0]])]});}
            var Q7;
            {var subQ3=sQuery(id+"F0.wireOp",EDGE,"E115");Q7=makeQuery(id+"F0.imprint","IMPRINT",FACE,{"disambiguationData":[TD([[makeQuery(id+"F0.imprint","IMPRINT",EDGE,{"derivedFrom":subQ3}),-1.0]])]});}
            var Q8;
            {var subQ3=sQuery(id+"F0.wireOp",EDGE,"E114");Q8=makeQuery(id+"F0.imprint","IMPRINT",FACE,{"disambiguationData":[TD([[makeQuery(id+"F0.imprint","IMPRINT",EDGE,{"derivedFrom":subQ3}),-1.0]])]});}
            var Q9;
            {var subQ3=sQuery(id+"F0.wireOp",EDGE,"E102");Q9=makeQuery(id+"F0.imprint","IMPRINT",FACE,{"disambiguationData":[TD([[makeQuery(id+"F0.imprint","IMPRINT",EDGE,{"derivedFrom":subQ3}),1.0]])]});}
            var Q10;
            {var subQ3=sQuery(id+"F0.wireOp",EDGE,"E101");Q10=makeQuery(id+"F0.imprint","IMPRINT",FACE,{"disambiguationData":[TD([[makeQuery(id+"F0.imprint","IMPRINT",EDGE,{"derivedFrom":subQ3}),1.0]])]});}
            var Q11;
            {var subQ3=sQuery(id+"F0.wireOp",EDGE,"E103");Q11=makeQuery(id+"F0.imprint","IMPRINT",FACE,{"disambiguationData":[TD([[makeQuery(id+"F0.imprint","IMPRINT",EDGE,{"derivedFrom":subQ3}),1.0]])]});}
            var Q12;
            {var subQ3=sQuery(id+"F0.wireOp",EDGE,"E100");Q12=makeQuery(id+"F0.imprint","IMPRINT",FACE,{"disambiguationData":[TD([[makeQuery(id+"F0.imprint","IMPRINT",EDGE,{"derivedFrom":subQ3}),-1.0]])]});}
            var Q13;
            {var subQ3=sQuery(id+"F0.wireOp",EDGE,"E99");Q13=makeQuery(id+"F0.imprint","IMPRINT",FACE,{"disambiguationData":[TD([[makeQuery(id+"F0.imprint","IMPRINT",EDGE,{"derivedFrom":subQ3}),-1.0]])]});}
            var Q14;
            {var subQ3=sQuery(id+"F0.wireOp",EDGE,"E98");Q14=makeQuery(id+"F0.imprint","IMPRINT",FACE,{"disambiguationData":[TD([[makeQuery(id+"F0.imprint","IMPRINT",EDGE,{"derivedFrom":subQ3}),-1.0]])]});}
            var Q15;
            {var subQ3=sQuery(id+"F0.wireOp",EDGE,"E106");Q15=makeQuery(id+"F0.imprint","IMPRINT",FACE,{"disambiguationData":[TD([[makeQuery(id+"F0.imprint","IMPRINT",EDGE,{"derivedFrom":subQ3}),-1.0]])]});}
            var Q16;
            {var subQ3=sQuery(id+"F0.wireOp",EDGE,"E104");Q16=makeQuery(id+"F0.imprint","IMPRINT",FACE,{"disambiguationData":[TD([[makeQuery(id+"F0.imprint","IMPRINT",EDGE,{"derivedFrom":subQ3}),-1.0]])]});}
            var Q17;
            {var subQ3=sQuery(id+"F0.wireOp",EDGE,"E105");Q17=makeQuery(id+"F0.imprint","IMPRINT",FACE,{"disambiguationData":[TD([[makeQuery(id+"F0.imprint","IMPRINT",EDGE,{"derivedFrom":subQ3}),-1.0]])]});}
            var Q18;
            {var subQ3=sQuery(id+"F0.wireOp",EDGE,"E117");Q18=makeQuery(id+"F0.imprint","IMPRINT",FACE,{"disambiguationData":[TD([[makeQuery(id+"F0.imprint","IMPRINT",EDGE,{"derivedFrom":subQ3}),1.0]])]});}
            var Q19;
            {var subQ3=sQuery(id+"F0.wireOp",EDGE,"E116");Q19=makeQuery(id+"F0.imprint","IMPRINT",FACE,{"disambiguationData":[TD([[makeQuery(id+"F0.imprint","IMPRINT",EDGE,{"derivedFrom":subQ3}),1.0]])]});}
            var Q20;
            {var subQ3=sQuery(id+"F0.wireOp",EDGE,"E118");Q20=makeQuery(id+"F0.imprint","IMPRINT",FACE,{"disambiguationData":[TD([[makeQuery(id+"F0.imprint","IMPRINT",EDGE,{"derivedFrom":subQ3}),1.0]])]});}
            var Q21;
            {var subQ3=sQuery(id+"F0.wireOp",EDGE,"E121");Q21=makeQuery(id+"F0.imprint","IMPRINT",FACE,{"disambiguationData":[TD([[makeQuery(id+"F0.imprint","IMPRINT",EDGE,{"derivedFrom":subQ3}),1.0]])]});}
            var Q22;
            {var subQ3=sQuery(id+"F0.wireOp",EDGE,"E120");Q22=makeQuery(id+"F0.imprint","IMPRINT",FACE,{"disambiguationData":[TD([[makeQuery(id+"F0.imprint","IMPRINT",EDGE,{"derivedFrom":subQ3}),1.0]])]});}
            var Q23;
            {var subQ3=sQuery(id+"F0.wireOp",EDGE,"E119");Q23=makeQuery(id+"F0.imprint","IMPRINT",FACE,{"disambiguationData":[TD([[makeQuery(id+"F0.imprint","IMPRINT",EDGE,{"derivedFrom":subQ3}),1.0]])]});}
            var Q24;
            {var subQ3=sQuery(id+"F0.wireOp",EDGE,"E122");Q24=makeQuery(id+"F0.imprint","IMPRINT",FACE,{"disambiguationData":[TD([[makeQuery(id+"F0.imprint","IMPRINT",EDGE,{"derivedFrom":subQ3}),-1.0]])]});}
            var Q25;
            {var subQ3=sQuery(id+"F0.wireOp",EDGE,"E124");Q25=makeQuery(id+"F0.imprint","IMPRINT",FACE,{"disambiguationData":[TD([[makeQuery(id+"F0.imprint","IMPRINT",EDGE,{"derivedFrom":subQ3}),-1.0]])]});}
            var Q26;
            {var subQ3=sQuery(id+"F0.wireOp",EDGE,"E123");Q26=makeQuery(id+"F0.imprint","IMPRINT",FACE,{"disambiguationData":[TD([[makeQuery(id+"F0.imprint","IMPRINT",EDGE,{"derivedFrom":subQ3}),-1.0]])]});}
            var Q27;
            {var subQ3=sQuery(id+"F0.wireOp",EDGE,"E68");Q27=makeQuery(id+"F0.imprint","IMPRINT",FACE,{"disambiguationData":[TD([[makeQuery(id+"F0.imprint","IMPRINT",EDGE,{"derivedFrom":subQ3}),-1.0]])]});}
            var Q28;
            {var subQ3=sQuery(id+"F0.wireOp",EDGE,"E70");Q28=makeQuery(id+"F0.imprint","IMPRINT",FACE,{"disambiguationData":[TD([[makeQuery(id+"F0.imprint","IMPRINT",EDGE,{"derivedFrom":subQ3}),-1.0]])]});}
            var Q29;
            {var subQ3=sQuery(id+"F0.wireOp",EDGE,"E69");Q29=makeQuery(id+"F0.imprint","IMPRINT",FACE,{"disambiguationData":[TD([[makeQuery(id+"F0.imprint","IMPRINT",EDGE,{"derivedFrom":subQ3}),-1.0]])]});}
            var Q30;
            {var subQ3=sQuery(id+"F0.wireOp",EDGE,"E72");Q30=makeQuery(id+"F0.imprint","IMPRINT",FACE,{"disambiguationData":[TD([[makeQuery(id+"F0.imprint","IMPRINT",EDGE,{"derivedFrom":subQ3}),-1.0]])]});}
            var Q31;
            {var subQ3=sQuery(id+"F0.wireOp",EDGE,"E74");Q31=makeQuery(id+"F0.imprint","IMPRINT",FACE,{"disambiguationData":[TD([[makeQuery(id+"F0.imprint","IMPRINT",EDGE,{"derivedFrom":subQ3}),-1.0]])]});}
            var Q32;
            {var subQ3=sQuery(id+"F0.wireOp",EDGE,"E73");Q32=makeQuery(id+"F0.imprint","IMPRINT",FACE,{"disambiguationData":[TD([[makeQuery(id+"F0.imprint","IMPRINT",EDGE,{"derivedFrom":subQ3}),-1.0]])]});}
            var Q33;
            {var subQ3=sQuery(id+"F0.wireOp",EDGE,"E87");Q33=makeQuery(id+"F0.imprint","IMPRINT",FACE,{"disambiguationData":[TD([[makeQuery(id+"F0.imprint","IMPRINT",EDGE,{"derivedFrom":subQ3}),-1.0]])]});}
            var Q34;
            {var subQ3=sQuery(id+"F0.wireOp",EDGE,"E85");Q34=makeQuery(id+"F0.imprint","IMPRINT",FACE,{"disambiguationData":[TD([[makeQuery(id+"F0.imprint","IMPRINT",EDGE,{"derivedFrom":subQ3}),-1.0]])]});}
            var Q35;
            {var subQ3=sQuery(id+"F0.wireOp",EDGE,"E86");Q35=makeQuery(id+"F0.imprint","IMPRINT",FACE,{"disambiguationData":[TD([[makeQuery(id+"F0.imprint","IMPRINT",EDGE,{"derivedFrom":subQ3}),-1.0]])]});}
            var Q36;
            {var subQ3=sQuery(id+"F0.wireOp",EDGE,"E89");Q36=makeQuery(id+"F0.imprint","IMPRINT",FACE,{"disambiguationData":[TD([[makeQuery(id+"F0.imprint","IMPRINT",EDGE,{"derivedFrom":subQ3}),1.0]])]});}
            var Q37;
            {var subQ3=sQuery(id+"F0.wireOp",EDGE,"E90");Q37=makeQuery(id+"F0.imprint","IMPRINT",FACE,{"disambiguationData":[TD([[makeQuery(id+"F0.imprint","IMPRINT",EDGE,{"derivedFrom":subQ3}),1.0]])]});}
            var Q38;
            {var subQ3=sQuery(id+"F0.wireOp",EDGE,"E88");Q38=makeQuery(id+"F0.imprint","IMPRINT",FACE,{"disambiguationData":[TD([[makeQuery(id+"F0.imprint","IMPRINT",EDGE,{"derivedFrom":subQ3}),1.0]])]});}
            var Q39;
            {var subQ3=sQuery(id+"F0.wireOp",EDGE,"E96");Q39=makeQuery(id+"F0.imprint","IMPRINT",FACE,{"disambiguationData":[TD([[makeQuery(id+"F0.imprint","IMPRINT",EDGE,{"derivedFrom":subQ3}),-1.0]])]});}
            var Q40;
            {var subQ3=sQuery(id+"F0.wireOp",EDGE,"E97");Q40=makeQuery(id+"F0.imprint","IMPRINT",FACE,{"disambiguationData":[TD([[makeQuery(id+"F0.imprint","IMPRINT",EDGE,{"derivedFrom":subQ3}),-1.0]])]});}
            var Q41;
            {var subQ3=sQuery(id+"F0.wireOp",EDGE,"E95");Q41=makeQuery(id+"F0.imprint","IMPRINT",FACE,{"disambiguationData":[TD([[makeQuery(id+"F0.imprint","IMPRINT",EDGE,{"derivedFrom":subQ3}),-1.0]])]});}
            var Q42;
            {var subQ3=sQuery(id+"F0.wireOp",EDGE,"E91");Q42=makeQuery(id+"F0.imprint","IMPRINT",FACE,{"disambiguationData":[TD([[makeQuery(id+"F0.imprint","IMPRINT",EDGE,{"derivedFrom":subQ3}),-1.0]])]});}
            var Q43;
            {var subQ3=sQuery(id+"F0.wireOp",EDGE,"E93");Q43=makeQuery(id+"F0.imprint","IMPRINT",FACE,{"disambiguationData":[TD([[makeQuery(id+"F0.imprint","IMPRINT",EDGE,{"derivedFrom":subQ3}),-1.0]])]});}
            var Q44;
            {var subQ3=sQuery(id+"F0.wireOp",EDGE,"E92");Q44=makeQuery(id+"F0.imprint","IMPRINT",FACE,{"disambiguationData":[TD([[makeQuery(id+"F0.imprint","IMPRINT",EDGE,{"derivedFrom":subQ3}),-1.0]])]});}
            var Q45;
            {var subQ3=sQuery(id+"F0.wireOp",EDGE,"E83");Q45=makeQuery(id+"F0.imprint","IMPRINT",FACE,{"disambiguationData":[TD([[makeQuery(id+"F0.imprint","IMPRINT",EDGE,{"derivedFrom":subQ3}),1.0]])]});}
            var Q46;
            {var subQ3=sQuery(id+"F0.wireOp",EDGE,"E84");Q46=makeQuery(id+"F0.imprint","IMPRINT",FACE,{"disambiguationData":[TD([[makeQuery(id+"F0.imprint","IMPRINT",EDGE,{"derivedFrom":subQ3}),1.0]])]});}
            var Q47;
            {var subQ3=sQuery(id+"F0.wireOp",EDGE,"E82");Q47=makeQuery(id+"F0.imprint","IMPRINT",FACE,{"disambiguationData":[TD([[makeQuery(id+"F0.imprint","IMPRINT",EDGE,{"derivedFrom":subQ3}),1.0]])]});}
            var Q48;
            {var subQ3=sQuery(id+"F0.wireOp",EDGE,"E81");Q48=makeQuery(id+"F0.imprint","IMPRINT",FACE,{"disambiguationData":[TD([[makeQuery(id+"F0.imprint","IMPRINT",EDGE,{"derivedFrom":subQ3}),1.0]])]});}
            var Q49;
            {var subQ3=sQuery(id+"F0.wireOp",EDGE,"E79");Q49=makeQuery(id+"F0.imprint","IMPRINT",FACE,{"disambiguationData":[TD([[makeQuery(id+"F0.imprint","IMPRINT",EDGE,{"derivedFrom":subQ3}),1.0]])]});}
            var Q50;
            {var subQ3=sQuery(id+"F0.wireOp",EDGE,"E80");Q50=makeQuery(id+"F0.imprint","IMPRINT",FACE,{"disambiguationData":[TD([[makeQuery(id+"F0.imprint","IMPRINT",EDGE,{"derivedFrom":subQ3}),1.0]])]});}
            var Q51;
            {var subQ3=sQuery(id+"F0.wireOp",EDGE,"E78");Q51=makeQuery(id+"F0.imprint","IMPRINT",FACE,{"disambiguationData":[TD([[makeQuery(id+"F0.imprint","IMPRINT",EDGE,{"derivedFrom":subQ3}),-1.0]])]});}
            var Q52;
            {var subQ3=sQuery(id+"F0.wireOp",EDGE,"E76");Q52=makeQuery(id+"F0.imprint","IMPRINT",FACE,{"disambiguationData":[TD([[makeQuery(id+"F0.imprint","IMPRINT",EDGE,{"derivedFrom":subQ3}),-1.0]])]});}
            var Q53;
            {var subQ3=sQuery(id+"F0.wireOp",EDGE,"E77");Q53=makeQuery(id+"F0.imprint","IMPRINT",FACE,{"disambiguationData":[TD([[makeQuery(id+"F0.imprint","IMPRINT",EDGE,{"derivedFrom":subQ3}),-1.0]])]});}
            var Q54;
            {var subQ3=sQuery(id+"F0.wireOp",EDGE,"E126");Q54=makeQuery(id+"F0.imprint","IMPRINT",FACE,{"disambiguationData":[TD([[makeQuery(id+"F0.imprint","IMPRINT",EDGE,{"derivedFrom":subQ3}),1.0]])]});}
            var Q55;
            {var subQ3=sQuery(id+"F0.wireOp",EDGE,"E127");Q55=makeQuery(id+"F0.imprint","IMPRINT",FACE,{"disambiguationData":[TD([[makeQuery(id+"F0.imprint","IMPRINT",EDGE,{"derivedFrom":subQ3}),1.0]])]});}
            var Q56;
            {var subQ3=sQuery(id+"F0.wireOp",EDGE,"E125");Q56=makeQuery(id+"F0.imprint","IMPRINT",FACE,{"disambiguationData":[TD([[makeQuery(id+"F0.imprint","IMPRINT",EDGE,{"derivedFrom":subQ3}),1.0]])]});}
            var Q57;
            {var subQ3=sQuery(id+"F0.wireOp",EDGE,"E133");Q57=makeQuery(id+"F0.imprint","IMPRINT",FACE,{"disambiguationData":[TD([[makeQuery(id+"F0.imprint","IMPRINT",EDGE,{"derivedFrom":subQ3}),1.0]])]});}
            var Q58;
            {var subQ3=sQuery(id+"F0.wireOp",EDGE,"E132");Q58=makeQuery(id+"F0.imprint","IMPRINT",FACE,{"disambiguationData":[TD([[makeQuery(id+"F0.imprint","IMPRINT",EDGE,{"derivedFrom":subQ3}),1.0]])]});}
            var Q59;
            {var subQ3=sQuery(id+"F0.wireOp",EDGE,"E131");Q59=makeQuery(id+"F0.imprint","IMPRINT",FACE,{"disambiguationData":[TD([[makeQuery(id+"F0.imprint","IMPRINT",EDGE,{"derivedFrom":subQ3}),1.0]])]});}
            var Q60;
            {var subQ3=sQuery(id+"F0.wireOp",EDGE,"E128");Q60=makeQuery(id+"F0.imprint","IMPRINT",FACE,{"disambiguationData":[TD([[makeQuery(id+"F0.imprint","IMPRINT",EDGE,{"derivedFrom":subQ3}),-1.0]])]});}
            var Q61;
            {var subQ3=sQuery(id+"F0.wireOp",EDGE,"E130");Q61=makeQuery(id+"F0.imprint","IMPRINT",FACE,{"disambiguationData":[TD([[makeQuery(id+"F0.imprint","IMPRINT",EDGE,{"derivedFrom":subQ3}),-1.0]])]});}
            var Q62;
            {var subQ3=sQuery(id+"F0.wireOp",EDGE,"E129");Q62=makeQuery(id+"F0.imprint","IMPRINT",FACE,{"disambiguationData":[TD([[makeQuery(id+"F0.imprint","IMPRINT",EDGE,{"derivedFrom":subQ3}),-1.0]])]});}
            var Q63;
            {var subQ3=sQuery(id+"F0.wireOp",EDGE,"E144");Q63=makeQuery(id+"F0.imprint","IMPRINT",FACE,{"disambiguationData":[TD([[makeQuery(id+"F0.imprint","IMPRINT",EDGE,{"derivedFrom":subQ3}),-1.0]])]});}
            var Q64;
            {var subQ3=sQuery(id+"F0.wireOp",EDGE,"E145");Q64=makeQuery(id+"F0.imprint","IMPRINT",FACE,{"disambiguationData":[TD([[makeQuery(id+"F0.imprint","IMPRINT",EDGE,{"derivedFrom":subQ3}),-1.0]])]});}
            var Q65;
            {var subQ3=sQuery(id+"F0.wireOp",EDGE,"E148");Q65=makeQuery(id+"F0.imprint","IMPRINT",FACE,{"disambiguationData":[TD([[makeQuery(id+"F0.imprint","IMPRINT",EDGE,{"derivedFrom":subQ3}),1.0]])]});}
            var Q66;
            {var subQ3=sQuery(id+"F0.wireOp",EDGE,"E147");Q66=makeQuery(id+"F0.imprint","IMPRINT",FACE,{"disambiguationData":[TD([[makeQuery(id+"F0.imprint","IMPRINT",EDGE,{"derivedFrom":subQ3}),1.0]])]});}
            var Q67;
            {var subQ3=sQuery(id+"F0.wireOp",EDGE,"E146");Q67=makeQuery(id+"F0.imprint","IMPRINT",FACE,{"disambiguationData":[TD([[makeQuery(id+"F0.imprint","IMPRINT",EDGE,{"derivedFrom":subQ3}),1.0]])]});}
            var Q68;
            {var subQ3=sQuery(id+"F0.wireOp",EDGE,"E143");Q68=makeQuery(id+"F0.imprint","IMPRINT",FACE,{"disambiguationData":[TD([[makeQuery(id+"F0.imprint","IMPRINT",EDGE,{"derivedFrom":subQ3}),-1.0]])]});}
            var Q69;
            {var subQ3=sQuery(id+"F0.wireOp",EDGE,"E151");Q69=makeQuery(id+"F0.imprint","IMPRINT",FACE,{"disambiguationData":[TD([[makeQuery(id+"F0.imprint","IMPRINT",EDGE,{"derivedFrom":subQ3}),1.0]])]});}
            var Q70;
            {var subQ3=sQuery(id+"F0.wireOp",EDGE,"E150");Q70=makeQuery(id+"F0.imprint","IMPRINT",FACE,{"disambiguationData":[TD([[makeQuery(id+"F0.imprint","IMPRINT",EDGE,{"derivedFrom":subQ3}),1.0]])]});}
            var Q71;
            {var subQ3=sQuery(id+"F0.wireOp",EDGE,"E149");Q71=makeQuery(id+"F0.imprint","IMPRINT",FACE,{"disambiguationData":[TD([[makeQuery(id+"F0.imprint","IMPRINT",EDGE,{"derivedFrom":subQ3}),1.0]])]});}
            var Q72;
            {var subQ3=sQuery(id+"F0.wireOp",EDGE,"E138");Q72=makeQuery(id+"F0.imprint","IMPRINT",FACE,{"disambiguationData":[TD([[makeQuery(id+"F0.imprint","IMPRINT",EDGE,{"derivedFrom":subQ3}),1.0]])]});}
            var Q73;
            {var subQ3=sQuery(id+"F0.wireOp",EDGE,"E137");Q73=makeQuery(id+"F0.imprint","IMPRINT",FACE,{"disambiguationData":[TD([[makeQuery(id+"F0.imprint","IMPRINT",EDGE,{"derivedFrom":subQ3}),1.0]])]});}
            var Q74;
            {var subQ3=sQuery(id+"F0.wireOp",EDGE,"E139");Q74=makeQuery(id+"F0.imprint","IMPRINT",FACE,{"disambiguationData":[TD([[makeQuery(id+"F0.imprint","IMPRINT",EDGE,{"derivedFrom":subQ3}),1.0]])]});}
            var Q75;
            {var subQ3=sQuery(id+"F0.wireOp",EDGE,"E134");Q75=makeQuery(id+"F0.imprint","IMPRINT",FACE,{"disambiguationData":[TD([[makeQuery(id+"F0.imprint","IMPRINT",EDGE,{"derivedFrom":subQ3}),1.0]])]});}
            var Q76;
            {var subQ3=sQuery(id+"F0.wireOp",EDGE,"E136");Q76=makeQuery(id+"F0.imprint","IMPRINT",FACE,{"disambiguationData":[TD([[makeQuery(id+"F0.imprint","IMPRINT",EDGE,{"derivedFrom":subQ3}),1.0]])]});}
            var Q77;
            {var subQ3=sQuery(id+"F0.wireOp",EDGE,"E135");Q77=makeQuery(id+"F0.imprint","IMPRINT",FACE,{"disambiguationData":[TD([[makeQuery(id+"F0.imprint","IMPRINT",EDGE,{"derivedFrom":subQ3}),1.0]])]});}
            var Q78;
            {var subQ3=sQuery(id+"F0.wireOp",EDGE,"E142");Q78=makeQuery(id+"F0.imprint","IMPRINT",FACE,{"disambiguationData":[TD([[makeQuery(id+"F0.imprint","IMPRINT",EDGE,{"derivedFrom":subQ3}),-1.0]])]});}
            var Q79;
            {var subQ3=sQuery(id+"F0.wireOp",EDGE,"E140");Q79=makeQuery(id+"F0.imprint","IMPRINT",FACE,{"disambiguationData":[TD([[makeQuery(id+"F0.imprint","IMPRINT",EDGE,{"derivedFrom":subQ3}),-1.0]])]});}
            var Q80;
            {var subQ3=sQuery(id+"F0.wireOp",EDGE,"E141");Q80=makeQuery(id+"F0.imprint","IMPRINT",FACE,{"disambiguationData":[TD([[makeQuery(id+"F0.imprint","IMPRINT",EDGE,{"derivedFrom":subQ3}),-1.0]])]});}
            var Q81;
            {var subQ3=sQuery(id+"F0.wireOp",EDGE,"E322");Q81=makeQuery(id+"F0.imprint","IMPRINT",FACE,{"disambiguationData":[TD([[makeQuery(id+"F0.imprint","IMPRINT",EDGE,{"derivedFrom":subQ3}),1.0]])]});}
            var Q82;
            {var subQ3=sQuery(id+"F0.wireOp",EDGE,"E323");Q82=makeQuery(id+"F0.imprint","IMPRINT",FACE,{"disambiguationData":[TD([[makeQuery(id+"F0.imprint","IMPRINT",EDGE,{"derivedFrom":subQ3}),1.0]])]});}
            var Q83;
            {var subQ3=sQuery(id+"F0.wireOp",EDGE,"E321");Q83=makeQuery(id+"F0.imprint","IMPRINT",FACE,{"disambiguationData":[TD([[makeQuery(id+"F0.imprint","IMPRINT",EDGE,{"derivedFrom":subQ3}),1.0]])]});}
            var Q84;
            {var subQ3=sQuery(id+"F0.wireOp",EDGE,"E336");Q84=makeQuery(id+"F0.imprint","IMPRINT",FACE,{"disambiguationData":[TD([[makeQuery(id+"F0.imprint","IMPRINT",EDGE,{"derivedFrom":subQ3}),-1.0]])]});}
            var Q85;
            {var subQ3=sQuery(id+"F0.wireOp",EDGE,"E338");Q85=makeQuery(id+"F0.imprint","IMPRINT",FACE,{"disambiguationData":[TD([[makeQuery(id+"F0.imprint","IMPRINT",EDGE,{"derivedFrom":subQ3}),-1.0]])]});}
            var Q86;
            {var subQ3=sQuery(id+"F0.wireOp",EDGE,"E337");Q86=makeQuery(id+"F0.imprint","IMPRINT",FACE,{"disambiguationData":[TD([[makeQuery(id+"F0.imprint","IMPRINT",EDGE,{"derivedFrom":subQ3}),-1.0]])]});}
            var Q87;
            {var subQ3=sQuery(id+"F0.wireOp",EDGE,"E326");Q87=makeQuery(id+"F0.imprint","IMPRINT",FACE,{"disambiguationData":[TD([[makeQuery(id+"F0.imprint","IMPRINT",EDGE,{"derivedFrom":subQ3}),-1.0]])]});}
            var Q88;
            {var subQ3=sQuery(id+"F0.wireOp",EDGE,"E325");Q88=makeQuery(id+"F0.imprint","IMPRINT",FACE,{"disambiguationData":[TD([[makeQuery(id+"F0.imprint","IMPRINT",EDGE,{"derivedFrom":subQ3}),-1.0]])]});}
            var Q89;
            {var subQ3=sQuery(id+"F0.wireOp",EDGE,"E324");Q89=makeQuery(id+"F0.imprint","IMPRINT",FACE,{"disambiguationData":[TD([[makeQuery(id+"F0.imprint","IMPRINT",EDGE,{"derivedFrom":subQ3}),-1.0]])]});}
            var Q90;
            {var subQ3=sQuery(id+"F0.wireOp",EDGE,"E328");Q90=makeQuery(id+"F0.imprint","IMPRINT",FACE,{"disambiguationData":[TD([[makeQuery(id+"F0.imprint","IMPRINT",EDGE,{"derivedFrom":subQ3}),1.0]])]});}
            var Q91;
            {var subQ3=sQuery(id+"F0.wireOp",EDGE,"E327");Q91=makeQuery(id+"F0.imprint","IMPRINT",FACE,{"disambiguationData":[TD([[makeQuery(id+"F0.imprint","IMPRINT",EDGE,{"derivedFrom":subQ3}),1.0]])]});}
            var Q92;
            {var subQ3=sQuery(id+"F0.wireOp",EDGE,"E329");Q92=makeQuery(id+"F0.imprint","IMPRINT",FACE,{"disambiguationData":[TD([[makeQuery(id+"F0.imprint","IMPRINT",EDGE,{"derivedFrom":subQ3}),1.0]])]});}
            var Q93;
            {var subQ3=sQuery(id+"F0.wireOp",EDGE,"E330");Q93=makeQuery(id+"F0.imprint","IMPRINT",FACE,{"disambiguationData":[TD([[makeQuery(id+"F0.imprint","IMPRINT",EDGE,{"derivedFrom":subQ3}),1.0]])]});}
            var Q94;
            {var subQ3=sQuery(id+"F0.wireOp",EDGE,"E332");Q94=makeQuery(id+"F0.imprint","IMPRINT",FACE,{"disambiguationData":[TD([[makeQuery(id+"F0.imprint","IMPRINT",EDGE,{"derivedFrom":subQ3}),1.0]])]});}
            var Q95;
            {var subQ3=sQuery(id+"F0.wireOp",EDGE,"E331");Q95=makeQuery(id+"F0.imprint","IMPRINT",FACE,{"disambiguationData":[TD([[makeQuery(id+"F0.imprint","IMPRINT",EDGE,{"derivedFrom":subQ3}),1.0]])]});}
            var Q96;
            {var subQ3=sQuery(id+"F0.wireOp",EDGE,"E335");Q96=makeQuery(id+"F0.imprint","IMPRINT",FACE,{"disambiguationData":[TD([[makeQuery(id+"F0.imprint","IMPRINT",EDGE,{"derivedFrom":subQ3}),-1.0]])]});}
            var Q97;
            {var subQ3=sQuery(id+"F0.wireOp",EDGE,"E333");Q97=makeQuery(id+"F0.imprint","IMPRINT",FACE,{"disambiguationData":[TD([[makeQuery(id+"F0.imprint","IMPRINT",EDGE,{"derivedFrom":subQ3}),-1.0]])]});}
            var Q98;
            {var subQ3=sQuery(id+"F0.wireOp",EDGE,"E334");Q98=makeQuery(id+"F0.imprint","IMPRINT",FACE,{"disambiguationData":[TD([[makeQuery(id+"F0.imprint","IMPRINT",EDGE,{"derivedFrom":subQ3}),-1.0]])]});}
            var Q99;
            {var subQ3=sQuery(id+"F0.wireOp",EDGE,"E340");Q99=makeQuery(id+"F0.imprint","IMPRINT",FACE,{"disambiguationData":[TD([[makeQuery(id+"F0.imprint","IMPRINT",EDGE,{"derivedFrom":subQ3}),1.0]])]});}
            var Q100;
            {var subQ3=sQuery(id+"F0.wireOp",EDGE,"E341");Q100=makeQuery(id+"F0.imprint","IMPRINT",FACE,{"disambiguationData":[TD([[makeQuery(id+"F0.imprint","IMPRINT",EDGE,{"derivedFrom":subQ3}),1.0]])]});}
            var Q101;
            {var subQ3=sQuery(id+"F0.wireOp",EDGE,"E339");Q101=makeQuery(id+"F0.imprint","IMPRINT",FACE,{"disambiguationData":[TD([[makeQuery(id+"F0.imprint","IMPRINT",EDGE,{"derivedFrom":subQ3}),1.0]])]});}
            var Q102;
            {var subQ3=sQuery(id+"F0.wireOp",EDGE,"E345");Q102=makeQuery(id+"F0.imprint","IMPRINT",FACE,{"disambiguationData":[TD([[makeQuery(id+"F0.imprint","IMPRINT",EDGE,{"derivedFrom":subQ3}),-1.0]])]});}
            var Q103;
            {var subQ3=sQuery(id+"F0.wireOp",EDGE,"E346");Q103=makeQuery(id+"F0.imprint","IMPRINT",FACE,{"disambiguationData":[TD([[makeQuery(id+"F0.imprint","IMPRINT",EDGE,{"derivedFrom":subQ3}),-1.0]])]});}
            var Q104;
            {var subQ3=sQuery(id+"F0.wireOp",EDGE,"E347");Q104=makeQuery(id+"F0.imprint","IMPRINT",FACE,{"disambiguationData":[TD([[makeQuery(id+"F0.imprint","IMPRINT",EDGE,{"derivedFrom":subQ3}),-1.0]])]});}
            var Q105;
            {var subQ3=sQuery(id+"F0.wireOp",EDGE,"E342");Q105=makeQuery(id+"F0.imprint","IMPRINT",FACE,{"disambiguationData":[TD([[makeQuery(id+"F0.imprint","IMPRINT",EDGE,{"derivedFrom":subQ3}),1.0]])]});}
            var Q106;
            {var subQ3=sQuery(id+"F0.wireOp",EDGE,"E343");Q106=makeQuery(id+"F0.imprint","IMPRINT",FACE,{"disambiguationData":[TD([[makeQuery(id+"F0.imprint","IMPRINT",EDGE,{"derivedFrom":subQ3}),1.0]])]});}
            var Q107;
            {var subQ3=sQuery(id+"F0.wireOp",EDGE,"E344");Q107=makeQuery(id+"F0.imprint","IMPRINT",FACE,{"disambiguationData":[TD([[makeQuery(id+"F0.imprint","IMPRINT",EDGE,{"derivedFrom":subQ3}),1.0]])]});}
            var Q108;
            {var subQ3=sQuery(id+"F0.wireOp",EDGE,"E298");Q108=makeQuery(id+"F0.imprint","IMPRINT",FACE,{"disambiguationData":[TD([[makeQuery(id+"F0.imprint","IMPRINT",EDGE,{"derivedFrom":subQ3}),-1.0]])]});}
            var Q109;
            {var subQ3=sQuery(id+"F0.wireOp",EDGE,"E299");Q109=makeQuery(id+"F0.imprint","IMPRINT",FACE,{"disambiguationData":[TD([[makeQuery(id+"F0.imprint","IMPRINT",EDGE,{"derivedFrom":subQ3}),-1.0]])]});}
            var Q110;
            {var subQ3=sQuery(id+"F0.wireOp",EDGE,"E297");Q110=makeQuery(id+"F0.imprint","IMPRINT",FACE,{"disambiguationData":[TD([[makeQuery(id+"F0.imprint","IMPRINT",EDGE,{"derivedFrom":subQ3}),-1.0]])]});}
            var Q111;
            {var subQ3=sQuery(id+"F0.wireOp",EDGE,"E296");Q111=makeQuery(id+"F0.imprint","IMPRINT",FACE,{"disambiguationData":[TD([[makeQuery(id+"F0.imprint","IMPRINT",EDGE,{"derivedFrom":subQ3}),1.0]])]});}
            var Q112;
            {var subQ3=sQuery(id+"F0.wireOp",EDGE,"E295");Q112=makeQuery(id+"F0.imprint","IMPRINT",FACE,{"disambiguationData":[TD([[makeQuery(id+"F0.imprint","IMPRINT",EDGE,{"derivedFrom":subQ3}),1.0]])]});}
            var Q113;
            {var subQ3=sQuery(id+"F0.wireOp",EDGE,"E294");Q113=makeQuery(id+"F0.imprint","IMPRINT",FACE,{"disambiguationData":[TD([[makeQuery(id+"F0.imprint","IMPRINT",EDGE,{"derivedFrom":subQ3}),1.0]])]});}
            var Q114;
            {var subQ3=sQuery(id+"F0.wireOp",EDGE,"E300");Q114=makeQuery(id+"F0.imprint","IMPRINT",FACE,{"disambiguationData":[TD([[makeQuery(id+"F0.imprint","IMPRINT",EDGE,{"derivedFrom":subQ3}),-1.0]])]});}
            var Q115;
            {var subQ3=sQuery(id+"F0.wireOp",EDGE,"E302");Q115=makeQuery(id+"F0.imprint","IMPRINT",FACE,{"disambiguationData":[TD([[makeQuery(id+"F0.imprint","IMPRINT",EDGE,{"derivedFrom":subQ3}),-1.0]])]});}
            var Q116;
            {var subQ3=sQuery(id+"F0.wireOp",EDGE,"E301");Q116=makeQuery(id+"F0.imprint","IMPRINT",FACE,{"disambiguationData":[TD([[makeQuery(id+"F0.imprint","IMPRINT",EDGE,{"derivedFrom":subQ3}),-1.0]])]});}
            var Q117;
            {var subQ3=sQuery(id+"F0.wireOp",EDGE,"E310");Q117=makeQuery(id+"F0.imprint","IMPRINT",FACE,{"disambiguationData":[TD([[makeQuery(id+"F0.imprint","IMPRINT",EDGE,{"derivedFrom":subQ3}),1.0]])]});}
            var Q118;
            {var subQ3=sQuery(id+"F0.wireOp",EDGE,"E309");Q118=makeQuery(id+"F0.imprint","IMPRINT",FACE,{"disambiguationData":[TD([[makeQuery(id+"F0.imprint","IMPRINT",EDGE,{"derivedFrom":subQ3}),1.0]])]});}
            var Q119;
            {var subQ3=sQuery(id+"F0.wireOp",EDGE,"E311");Q119=makeQuery(id+"F0.imprint","IMPRINT",FACE,{"disambiguationData":[TD([[makeQuery(id+"F0.imprint","IMPRINT",EDGE,{"derivedFrom":subQ3}),1.0]])]});}
            var Q120;
            {var subQ3=sQuery(id+"F0.wireOp",EDGE,"E290");Q120=makeQuery(id+"F0.imprint","IMPRINT",FACE,{"disambiguationData":[TD([[makeQuery(id+"F0.imprint","IMPRINT",EDGE,{"derivedFrom":subQ3}),-1.0]])]});}
            var Q121;
            {var subQ3=sQuery(id+"F0.wireOp",EDGE,"E288");Q121=makeQuery(id+"F0.imprint","IMPRINT",FACE,{"disambiguationData":[TD([[makeQuery(id+"F0.imprint","IMPRINT",EDGE,{"derivedFrom":subQ3}),-1.0]])]});}
            var Q122;
            {var subQ3=sQuery(id+"F0.wireOp",EDGE,"E289");Q122=makeQuery(id+"F0.imprint","IMPRINT",FACE,{"disambiguationData":[TD([[makeQuery(id+"F0.imprint","IMPRINT",EDGE,{"derivedFrom":subQ3}),-1.0]])]});}
            var Q123;
            {var subQ3=sQuery(id+"F0.wireOp",EDGE,"E307");Q123=makeQuery(id+"F0.imprint","IMPRINT",FACE,{"disambiguationData":[TD([[makeQuery(id+"F0.imprint","IMPRINT",EDGE,{"derivedFrom":subQ3}),-1.0]])]});}
            var Q124;
            {var subQ3=sQuery(id+"F0.wireOp",EDGE,"E308");Q124=makeQuery(id+"F0.imprint","IMPRINT",FACE,{"disambiguationData":[TD([[makeQuery(id+"F0.imprint","IMPRINT",EDGE,{"derivedFrom":subQ3}),-1.0]])]});}
            var Q125;
            {var subQ3=sQuery(id+"F0.wireOp",EDGE,"E306");Q125=makeQuery(id+"F0.imprint","IMPRINT",FACE,{"disambiguationData":[TD([[makeQuery(id+"F0.imprint","IMPRINT",EDGE,{"derivedFrom":subQ3}),-1.0]])]});}
            var Q126;
            {var subQ3=sQuery(id+"F0.wireOp",EDGE,"E292");Q126=makeQuery(id+"F0.imprint","IMPRINT",FACE,{"disambiguationData":[TD([[makeQuery(id+"F0.imprint","IMPRINT",EDGE,{"derivedFrom":subQ3}),-1.0]])]});}
            var Q127;
            {var subQ3=sQuery(id+"F0.wireOp",EDGE,"E293");Q127=makeQuery(id+"F0.imprint","IMPRINT",FACE,{"disambiguationData":[TD([[makeQuery(id+"F0.imprint","IMPRINT",EDGE,{"derivedFrom":subQ3}),-1.0]])]});}
            var Q128;
            {var subQ3=sQuery(id+"F0.wireOp",EDGE,"E291");Q128=makeQuery(id+"F0.imprint","IMPRINT",FACE,{"disambiguationData":[TD([[makeQuery(id+"F0.imprint","IMPRINT",EDGE,{"derivedFrom":subQ3}),-1.0]])]});}
            var Q129;
            {var subQ3=sQuery(id+"F0.wireOp",EDGE,"E305");Q129=makeQuery(id+"F0.imprint","IMPRINT",FACE,{"disambiguationData":[TD([[makeQuery(id+"F0.imprint","IMPRINT",EDGE,{"derivedFrom":subQ3}),1.0]])]});}
            var Q130;
            {var subQ3=sQuery(id+"F0.wireOp",EDGE,"E304");Q130=makeQuery(id+"F0.imprint","IMPRINT",FACE,{"disambiguationData":[TD([[makeQuery(id+"F0.imprint","IMPRINT",EDGE,{"derivedFrom":subQ3}),1.0]])]});}
            var Q131;
            {var subQ3=sQuery(id+"F0.wireOp",EDGE,"E303");Q131=makeQuery(id+"F0.imprint","IMPRINT",FACE,{"disambiguationData":[TD([[makeQuery(id+"F0.imprint","IMPRINT",EDGE,{"derivedFrom":subQ3}),1.0]])]});}
            var Q132;
            {var subQ3=sQuery(id+"F0.wireOp",EDGE,"E319");Q132=makeQuery(id+"F0.imprint","IMPRINT",FACE,{"disambiguationData":[TD([[makeQuery(id+"F0.imprint","IMPRINT",EDGE,{"derivedFrom":subQ3}),1.0]])]});}
            var Q133;
            {var subQ3=sQuery(id+"F0.wireOp",EDGE,"E312");Q133=makeQuery(id+"F0.imprint","IMPRINT",FACE,{"disambiguationData":[TD([[makeQuery(id+"F0.imprint","IMPRINT",EDGE,{"derivedFrom":subQ3}),-1.0]])]});}
            var Q134;
            {var subQ3=sQuery(id+"F0.wireOp",EDGE,"E314");Q134=makeQuery(id+"F0.imprint","IMPRINT",FACE,{"disambiguationData":[TD([[makeQuery(id+"F0.imprint","IMPRINT",EDGE,{"derivedFrom":subQ3}),-1.0]])]});}
            var Q135;
            {var subQ3=sQuery(id+"F0.wireOp",EDGE,"E313");Q135=makeQuery(id+"F0.imprint","IMPRINT",FACE,{"disambiguationData":[TD([[makeQuery(id+"F0.imprint","IMPRINT",EDGE,{"derivedFrom":subQ3}),-1.0]])]});}
            var Q136;
            {var subQ3=sQuery(id+"F0.wireOp",EDGE,"E320");Q136=makeQuery(id+"F0.imprint","IMPRINT",FACE,{"disambiguationData":[TD([[makeQuery(id+"F0.imprint","IMPRINT",EDGE,{"derivedFrom":subQ3}),1.0]])]});}
            var Q137;
            {var subQ3=sQuery(id+"F0.wireOp",EDGE,"E315");Q137=makeQuery(id+"F0.imprint","IMPRINT",FACE,{"disambiguationData":[TD([[makeQuery(id+"F0.imprint","IMPRINT",EDGE,{"derivedFrom":subQ3}),1.0]])]});}
            var Q138;
            {var subQ3=sQuery(id+"F0.wireOp",EDGE,"E317");Q138=makeQuery(id+"F0.imprint","IMPRINT",FACE,{"disambiguationData":[TD([[makeQuery(id+"F0.imprint","IMPRINT",EDGE,{"derivedFrom":subQ3}),1.0]])]});}
            var Q139;
            {var subQ3=sQuery(id+"F0.wireOp",EDGE,"E316");Q139=makeQuery(id+"F0.imprint","IMPRINT",FACE,{"disambiguationData":[TD([[makeQuery(id+"F0.imprint","IMPRINT",EDGE,{"derivedFrom":subQ3}),1.0]])]});}
            var Q140;
            {var subQ3=sQuery(id+"F0.wireOp",EDGE,"E318");Q140=makeQuery(id+"F0.imprint","IMPRINT",FACE,{"disambiguationData":[TD([[makeQuery(id+"F0.imprint","IMPRINT",EDGE,{"derivedFrom":subQ3}),1.0]])]});}
            var Q141;
            {var subQ3=sQuery(id+"F0.wireOp",EDGE,"E357");Q141=makeQuery(id+"F0.imprint","IMPRINT",FACE,{"disambiguationData":[TD([[makeQuery(id+"F0.imprint","IMPRINT",EDGE,{"derivedFrom":subQ3}),-1.0]])]});}
            var Q142;
            {var subQ3=sQuery(id+"F0.wireOp",EDGE,"E359");Q142=makeQuery(id+"F0.imprint","IMPRINT",FACE,{"disambiguationData":[TD([[makeQuery(id+"F0.imprint","IMPRINT",EDGE,{"derivedFrom":subQ3}),-1.0]])]});}
            var Q143;
            {var subQ3=sQuery(id+"F0.wireOp",EDGE,"E358");Q143=makeQuery(id+"F0.imprint","IMPRINT",FACE,{"disambiguationData":[TD([[makeQuery(id+"F0.imprint","IMPRINT",EDGE,{"derivedFrom":subQ3}),-1.0]])]});}
            var Q144;
            {var subQ3=sQuery(id+"F0.wireOp",EDGE,"E365");Q144=makeQuery(id+"F0.imprint","IMPRINT",FACE,{"disambiguationData":[TD([[makeQuery(id+"F0.imprint","IMPRINT",EDGE,{"derivedFrom":subQ3}),-1.0]])]});}
            var Q145;
            {var subQ3=sQuery(id+"F0.wireOp",EDGE,"E364");Q145=makeQuery(id+"F0.imprint","IMPRINT",FACE,{"disambiguationData":[TD([[makeQuery(id+"F0.imprint","IMPRINT",EDGE,{"derivedFrom":subQ3}),-1.0]])]});}
            var Q146;
            {var subQ3=sQuery(id+"F0.wireOp",EDGE,"E363");Q146=makeQuery(id+"F0.imprint","IMPRINT",FACE,{"disambiguationData":[TD([[makeQuery(id+"F0.imprint","IMPRINT",EDGE,{"derivedFrom":subQ3}),1.0]])]});}
            var Q147;
            {var subQ3=sQuery(id+"F0.wireOp",EDGE,"E366");Q147=makeQuery(id+"F0.imprint","IMPRINT",FACE,{"disambiguationData":[TD([[makeQuery(id+"F0.imprint","IMPRINT",EDGE,{"derivedFrom":subQ3}),-1.0]])]});}
            var Q148;
            {var subQ3=sQuery(id+"F0.wireOp",EDGE,"E368");Q148=makeQuery(id+"F0.imprint","IMPRINT",FACE,{"disambiguationData":[TD([[makeQuery(id+"F0.imprint","IMPRINT",EDGE,{"derivedFrom":subQ3}),-1.0]])]});}
            var Q149;
            {var subQ3=sQuery(id+"F0.wireOp",EDGE,"E367");Q149=makeQuery(id+"F0.imprint","IMPRINT",FACE,{"disambiguationData":[TD([[makeQuery(id+"F0.imprint","IMPRINT",EDGE,{"derivedFrom":subQ3}),-1.0]])]});}
            var Q150;
            {var subQ3=sQuery(id+"F0.wireOp",EDGE,"E362");Q150=makeQuery(id+"F0.imprint","IMPRINT",FACE,{"disambiguationData":[TD([[makeQuery(id+"F0.imprint","IMPRINT",EDGE,{"derivedFrom":subQ3}),-1.0]])]});}
            var Q151;
            {var subQ3=sQuery(id+"F0.wireOp",EDGE,"E360");Q151=makeQuery(id+"F0.imprint","IMPRINT",FACE,{"disambiguationData":[TD([[makeQuery(id+"F0.imprint","IMPRINT",EDGE,{"derivedFrom":subQ3}),-1.0]])]});}
            var Q152;
            {var subQ3=sQuery(id+"F0.wireOp",EDGE,"E361");Q152=makeQuery(id+"F0.imprint","IMPRINT",FACE,{"disambiguationData":[TD([[makeQuery(id+"F0.imprint","IMPRINT",EDGE,{"derivedFrom":subQ3}),-1.0]])]});}
            var Q153;
            {var subQ3=sQuery(id+"F0.wireOp",EDGE,"E355");Q153=makeQuery(id+"F0.imprint","IMPRINT",FACE,{"disambiguationData":[TD([[makeQuery(id+"F0.imprint","IMPRINT",EDGE,{"derivedFrom":subQ3}),-1.0]])]});}
            var Q154;
            {var subQ3=sQuery(id+"F0.wireOp",EDGE,"E354");Q154=makeQuery(id+"F0.imprint","IMPRINT",FACE,{"disambiguationData":[TD([[makeQuery(id+"F0.imprint","IMPRINT",EDGE,{"derivedFrom":subQ3}),-1.0]])]});}
            var Q155;
            {var subQ3=sQuery(id+"F0.wireOp",EDGE,"E356");Q155=makeQuery(id+"F0.imprint","IMPRINT",FACE,{"disambiguationData":[TD([[makeQuery(id+"F0.imprint","IMPRINT",EDGE,{"derivedFrom":subQ3}),-1.0]])]});}
            var Q156;
            {var subQ3=sQuery(id+"F0.wireOp",EDGE,"E352");Q156=makeQuery(id+"F0.imprint","IMPRINT",FACE,{"disambiguationData":[TD([[makeQuery(id+"F0.imprint","IMPRINT",EDGE,{"derivedFrom":subQ3}),-1.0]])]});}
            var Q157;
            {var subQ3=sQuery(id+"F0.wireOp",EDGE,"E353");Q157=makeQuery(id+"F0.imprint","IMPRINT",FACE,{"disambiguationData":[TD([[makeQuery(id+"F0.imprint","IMPRINT",EDGE,{"derivedFrom":subQ3}),-1.0]])]});}
            var Q158;
            {var subQ3=sQuery(id+"F0.wireOp",EDGE,"E351");Q158=makeQuery(id+"F0.imprint","IMPRINT",FACE,{"disambiguationData":[TD([[makeQuery(id+"F0.imprint","IMPRINT",EDGE,{"derivedFrom":subQ3}),-1.0]])]});}
            var Q159;
            {var subQ3=sQuery(id+"F0.wireOp",EDGE,"E348");Q159=makeQuery(id+"F0.imprint","IMPRINT",FACE,{"disambiguationData":[TD([[makeQuery(id+"F0.imprint","IMPRINT",EDGE,{"derivedFrom":subQ3}),-1.0]])]});}
            var Q160;
            {var subQ3=sQuery(id+"F0.wireOp",EDGE,"E349");Q160=makeQuery(id+"F0.imprint","IMPRINT",FACE,{"disambiguationData":[TD([[makeQuery(id+"F0.imprint","IMPRINT",EDGE,{"derivedFrom":subQ3}),-1.0]])]});}
            var Q161;
            {var subQ3=sQuery(id+"F0.wireOp",EDGE,"E350");Q161=makeQuery(id+"F0.imprint","IMPRINT",FACE,{"disambiguationData":[TD([[makeQuery(id+"F0.imprint","IMPRINT",EDGE,{"derivedFrom":subQ3}),-1.0]])]});}
            var Q162;
            {var subQ0=sQuery(id+"F0.wireOp",EDGE,"E203.MirrorCS");Q162=makeQuery(id+"F0.imprint","IMPRINT",FACE,{"disambiguationData":[TD([[makeQuery(id+"F0.imprint","IMPRINT",EDGE,{"derivedFrom":subQ0}),1.0]])]});}
            var Q163;
            {var subQ3=sQuery(id+"F0.wireOp",EDGE,"E204.MirrorCS");Q163=makeQuery(id+"F0.imprint","IMPRINT",FACE,{"disambiguationData":[TD([[makeQuery(id+"F0.imprint","IMPRINT",EDGE,{"derivedFrom":subQ3}),1.0]])]});}
            var Q164;
            {var subQ0=sQuery(id+"F0.wireOp",EDGE,"E205.MirrorCS");Q164=makeQuery(id+"F0.imprint","IMPRINT",FACE,{"disambiguationData":[TD([[makeQuery(id+"F0.imprint","IMPRINT",EDGE,{"derivedFrom":subQ0}),1.0]])]});}
            var Q165;
            {var subQ0=sQuery(id+"F0.wireOp",EDGE,"E200.MirrorCS");Q165=makeQuery(id+"F0.imprint","IMPRINT",FACE,{"disambiguationData":[TD([[makeQuery(id+"F0.imprint","IMPRINT",EDGE,{"derivedFrom":subQ0}),-1.0]])]});}
            var Q166;
            {var subQ3=sQuery(id+"F0.wireOp",EDGE,"E202.MirrorCS");Q166=makeQuery(id+"F0.imprint","IMPRINT",FACE,{"disambiguationData":[TD([[makeQuery(id+"F0.imprint","IMPRINT",EDGE,{"derivedFrom":subQ3}),-1.0]])]});}
            var Q167;
            {var subQ0=sQuery(id+"F0.wireOp",EDGE,"E201.MirrorCS");Q167=makeQuery(id+"F0.imprint","IMPRINT",FACE,{"disambiguationData":[TD([[makeQuery(id+"F0.imprint","IMPRINT",EDGE,{"derivedFrom":subQ0}),-1.0]])]});}
            var Q168;
            {var subQ3=sQuery(id+"F0.wireOp",EDGE,"E209.MirrorCS");Q168=makeQuery(id+"F0.imprint","IMPRINT",FACE,{"disambiguationData":[TD([[makeQuery(id+"F0.imprint","IMPRINT",EDGE,{"derivedFrom":subQ3}),-1.0]])]});}
            var Q169;
            {var subQ3=sQuery(id+"F0.wireOp",EDGE,"E211.MirrorCS");Q169=makeQuery(id+"F0.imprint","IMPRINT",FACE,{"disambiguationData":[TD([[makeQuery(id+"F0.imprint","IMPRINT",EDGE,{"derivedFrom":subQ3}),-1.0]])]});}
            var Q170;
            {var subQ3=sQuery(id+"F0.wireOp",EDGE,"E210.MirrorCS");Q170=makeQuery(id+"F0.imprint","IMPRINT",FACE,{"disambiguationData":[TD([[makeQuery(id+"F0.imprint","IMPRINT",EDGE,{"derivedFrom":subQ3}),-1.0]])]});}
            var Q171;
            {var subQ3=sQuery(id+"F0.wireOp",EDGE,"E212.MirrorCS");Q171=makeQuery(id+"F0.imprint","IMPRINT",FACE,{"disambiguationData":[TD([[makeQuery(id+"F0.imprint","IMPRINT",EDGE,{"derivedFrom":subQ3}),-1.0]])]});}
            var Q172;
            {var subQ0=sQuery(id+"F0.wireOp",EDGE,"E213.MirrorCS");Q172=makeQuery(id+"F0.imprint","IMPRINT",FACE,{"disambiguationData":[TD([[makeQuery(id+"F0.imprint","IMPRINT",EDGE,{"derivedFrom":subQ0}),-1.0]])]});}
            var Q173;
            {var subQ0=sQuery(id+"F0.wireOp",EDGE,"E219.MirrorCS");Q173=makeQuery(id+"F0.imprint","IMPRINT",FACE,{"disambiguationData":[TD([[makeQuery(id+"F0.imprint","IMPRINT",EDGE,{"derivedFrom":subQ0}),-1.0]])]});}
            var Q174;
            {var subQ3=sQuery(id+"F0.wireOp",EDGE,"E220.MirrorCS");Q174=makeQuery(id+"F0.imprint","IMPRINT",FACE,{"disambiguationData":[TD([[makeQuery(id+"F0.imprint","IMPRINT",EDGE,{"derivedFrom":subQ3}),1.0]])]});}
            var Q175;
            {var subQ3=sQuery(id+"F0.wireOp",EDGE,"E221.MirrorCS");Q175=makeQuery(id+"F0.imprint","IMPRINT",FACE,{"disambiguationData":[TD([[makeQuery(id+"F0.imprint","IMPRINT",EDGE,{"derivedFrom":subQ3}),1.0]])]});}
            var Q176;
            {var subQ3=sQuery(id+"F0.wireOp",EDGE,"E222.MirrorCS");Q176=makeQuery(id+"F0.imprint","IMPRINT",FACE,{"disambiguationData":[TD([[makeQuery(id+"F0.imprint","IMPRINT",EDGE,{"derivedFrom":subQ3}),1.0]])]});}
            var Q177;
            {var subQ3=sQuery(id+"F0.wireOp",EDGE,"E218.MirrorCS");Q177=makeQuery(id+"F0.imprint","IMPRINT",FACE,{"disambiguationData":[TD([[makeQuery(id+"F0.imprint","IMPRINT",EDGE,{"derivedFrom":subQ3}),-1.0]])]});}
            var Q178;
            {var subQ3=sQuery(id+"F0.wireOp",EDGE,"E216.MirrorCS");Q178=makeQuery(id+"F0.imprint","IMPRINT",FACE,{"disambiguationData":[TD([[makeQuery(id+"F0.imprint","IMPRINT",EDGE,{"derivedFrom":subQ3}),-1.0]])]});}
            var Q179;
            {var subQ3=sQuery(id+"F0.wireOp",EDGE,"E217.MirrorCS");Q179=makeQuery(id+"F0.imprint","IMPRINT",FACE,{"disambiguationData":[TD([[makeQuery(id+"F0.imprint","IMPRINT",EDGE,{"derivedFrom":subQ3}),-1.0]])]});}
            var Q180;
            {var subQ3=sQuery(id+"F0.wireOp",EDGE,"E199.MirrorCS");Q180=makeQuery(id+"F0.imprint","IMPRINT",FACE,{"disambiguationData":[TD([[makeQuery(id+"F0.imprint","IMPRINT",EDGE,{"derivedFrom":subQ3}),-1.0]])]});}
            var Q181;
            {var subQ3=sQuery(id+"F0.wireOp",EDGE,"E197.MirrorCS");Q181=makeQuery(id+"F0.imprint","IMPRINT",FACE,{"disambiguationData":[TD([[makeQuery(id+"F0.imprint","IMPRINT",EDGE,{"derivedFrom":subQ3}),-1.0]])]});}
            var Q182;
            {var subQ3=sQuery(id+"F0.wireOp",EDGE,"E193.MirrorCS");Q182=makeQuery(id+"F0.imprint","IMPRINT",FACE,{"disambiguationData":[TD([[makeQuery(id+"F0.imprint","IMPRINT",EDGE,{"derivedFrom":subQ3}),-1.0]])]});}
            var Q183;
            {var subQ3=sQuery(id+"F0.wireOp",EDGE,"E195.MirrorCS");Q183=makeQuery(id+"F0.imprint","IMPRINT",FACE,{"disambiguationData":[TD([[makeQuery(id+"F0.imprint","IMPRINT",EDGE,{"derivedFrom":subQ3}),-1.0]])]});}
            var Q184;
            {var subQ3=sQuery(id+"F0.wireOp",EDGE,"E194.MirrorCS");Q184=makeQuery(id+"F0.imprint","IMPRINT",FACE,{"disambiguationData":[TD([[makeQuery(id+"F0.imprint","IMPRINT",EDGE,{"derivedFrom":subQ3}),-1.0]])]});}
            var Q185;
            {var subQ0=sQuery(id+"F0.wireOp",EDGE,"E188.MirrorCS");Q185=makeQuery(id+"F0.imprint","IMPRINT",FACE,{"disambiguationData":[TD([[makeQuery(id+"F0.imprint","IMPRINT",EDGE,{"derivedFrom":subQ0}),1.0]])]});}
            var Q186;
            {var subQ3=sQuery(id+"F0.wireOp",EDGE,"E189.MirrorCS");Q186=makeQuery(id+"F0.imprint","IMPRINT",FACE,{"disambiguationData":[TD([[makeQuery(id+"F0.imprint","IMPRINT",EDGE,{"derivedFrom":subQ3}),1.0]])]});}
            var Q187;
            {var subQ0=sQuery(id+"F0.wireOp",EDGE,"E190.MirrorCS");Q187=makeQuery(id+"F0.imprint","IMPRINT",FACE,{"disambiguationData":[TD([[makeQuery(id+"F0.imprint","IMPRINT",EDGE,{"derivedFrom":subQ0}),1.0]])]});}
            var Q188;
            {var subQ3=sQuery(id+"F0.wireOp",EDGE,"E198.MirrorCS");Q188=makeQuery(id+"F0.imprint","IMPRINT",FACE,{"disambiguationData":[TD([[makeQuery(id+"F0.imprint","IMPRINT",EDGE,{"derivedFrom":subQ3}),-1.0]])]});}
            var Q189;
            {var subQ3=sQuery(id+"F0.wireOp",EDGE,"E258.MirrorCS");Q189=makeQuery(id+"F0.imprint","IMPRINT",FACE,{"disambiguationData":[TD([[makeQuery(id+"F0.imprint","IMPRINT",EDGE,{"derivedFrom":subQ3}),1.0]])]});}
            var Q190;
            {var subQ3=sQuery(id+"F0.wireOp",EDGE,"E256.MirrorCS");Q190=makeQuery(id+"F0.imprint","IMPRINT",FACE,{"disambiguationData":[TD([[makeQuery(id+"F0.imprint","IMPRINT",EDGE,{"derivedFrom":subQ3}),1.0]])]});}
            var Q191;
            {var subQ3=sQuery(id+"F0.wireOp",EDGE,"E257.MirrorCS");Q191=makeQuery(id+"F0.imprint","IMPRINT",FACE,{"disambiguationData":[TD([[makeQuery(id+"F0.imprint","IMPRINT",EDGE,{"derivedFrom":subQ3}),1.0]])]});}
            var Q192;
            {var subQ0=sQuery(id+"F0.wireOp",EDGE,"E250.MirrorCS");Q192=makeQuery(id+"F0.imprint","IMPRINT",FACE,{"disambiguationData":[TD([[makeQuery(id+"F0.imprint","IMPRINT",EDGE,{"derivedFrom":subQ0}),-1.0]])]});}
            var Q193;
            {var subQ0=sQuery(id+"F0.wireOp",EDGE,"E248.MirrorCS");Q193=makeQuery(id+"F0.imprint","IMPRINT",FACE,{"disambiguationData":[TD([[makeQuery(id+"F0.imprint","IMPRINT",EDGE,{"derivedFrom":subQ0}),-1.0]])]});}
            var Q194;
            {var subQ3=sQuery(id+"F0.wireOp",EDGE,"E249.MirrorCS");Q194=makeQuery(id+"F0.imprint","IMPRINT",FACE,{"disambiguationData":[TD([[makeQuery(id+"F0.imprint","IMPRINT",EDGE,{"derivedFrom":subQ3}),-1.0]])]});}
            var Q195;
            {var subQ3=sQuery(id+"F0.wireOp",EDGE,"E253.MirrorCS");Q195=makeQuery(id+"F0.imprint","IMPRINT",FACE,{"disambiguationData":[TD([[makeQuery(id+"F0.imprint","IMPRINT",EDGE,{"derivedFrom":subQ3}),-1.0]])]});}
            var Q196;
            {var subQ3=sQuery(id+"F0.wireOp",EDGE,"E255.MirrorCS");Q196=makeQuery(id+"F0.imprint","IMPRINT",FACE,{"disambiguationData":[TD([[makeQuery(id+"F0.imprint","IMPRINT",EDGE,{"derivedFrom":subQ3}),-1.0]])]});}
            var Q197;
            {var subQ3=sQuery(id+"F0.wireOp",EDGE,"E254.MirrorCS");Q197=makeQuery(id+"F0.imprint","IMPRINT",FACE,{"disambiguationData":[TD([[makeQuery(id+"F0.imprint","IMPRINT",EDGE,{"derivedFrom":subQ3}),-1.0]])]});}
            var Q198;
            {var subQ3=sQuery(id+"F0.wireOp",EDGE,"E235.MirrorCS");Q198=makeQuery(id+"F0.imprint","IMPRINT",FACE,{"disambiguationData":[TD([[makeQuery(id+"F0.imprint","IMPRINT",EDGE,{"derivedFrom":subQ3}),1.0]])]});}
            var Q199;
            {var subQ3=sQuery(id+"F0.wireOp",EDGE,"E234.MirrorCS");Q199=makeQuery(id+"F0.imprint","IMPRINT",FACE,{"disambiguationData":[TD([[makeQuery(id+"F0.imprint","IMPRINT",EDGE,{"derivedFrom":subQ3}),1.0]])]});}
            var Q200;
            {var subQ3=sQuery(id+"F0.wireOp",EDGE,"E233.MirrorCS");Q200=makeQuery(id+"F0.imprint","IMPRINT",FACE,{"disambiguationData":[TD([[makeQuery(id+"F0.imprint","IMPRINT",EDGE,{"derivedFrom":subQ3}),1.0]])]});}
            var Q201;
            {var subQ0=sQuery(id+"F0.wireOp",EDGE,"E226.MirrorCS");Q201=makeQuery(id+"F0.imprint","IMPRINT",FACE,{"disambiguationData":[TD([[makeQuery(id+"F0.imprint","IMPRINT",EDGE,{"derivedFrom":subQ0}),1.0]])]});}
            var Q202;
            {var subQ3=sQuery(id+"F0.wireOp",EDGE,"E225.MirrorCS");Q202=makeQuery(id+"F0.imprint","IMPRINT",FACE,{"disambiguationData":[TD([[makeQuery(id+"F0.imprint","IMPRINT",EDGE,{"derivedFrom":subQ3}),1.0]])]});}
            var Q203;
            {var subQ0=sQuery(id+"F0.wireOp",EDGE,"E224.MirrorCS");Q203=makeQuery(id+"F0.imprint","IMPRINT",FACE,{"disambiguationData":[TD([[makeQuery(id+"F0.imprint","IMPRINT",EDGE,{"derivedFrom":subQ0}),1.0]])]});}
            var Q204;
            {var subQ3=sQuery(id+"F0.wireOp",EDGE,"E231.MirrorCS");Q204=makeQuery(id+"F0.imprint","IMPRINT",FACE,{"disambiguationData":[TD([[makeQuery(id+"F0.imprint","IMPRINT",EDGE,{"derivedFrom":subQ3}),1.0]])]});}
            var Q205;
            {var subQ3=sQuery(id+"F0.wireOp",EDGE,"E229.MirrorCS");Q205=makeQuery(id+"F0.imprint","IMPRINT",FACE,{"disambiguationData":[TD([[makeQuery(id+"F0.imprint","IMPRINT",EDGE,{"derivedFrom":subQ3}),1.0]])]});}
            var Q206;
            {var subQ3=sQuery(id+"F0.wireOp",EDGE,"E230.MirrorCS");Q206=makeQuery(id+"F0.imprint","IMPRINT",FACE,{"disambiguationData":[TD([[makeQuery(id+"F0.imprint","IMPRINT",EDGE,{"derivedFrom":subQ3}),1.0]])]});}
            var Q207;
            {var subQ3=sQuery(id+"F0.wireOp",EDGE,"E242.MirrorCS");Q207=makeQuery(id+"F0.imprint","IMPRINT",FACE,{"disambiguationData":[TD([[makeQuery(id+"F0.imprint","IMPRINT",EDGE,{"derivedFrom":subQ3}),1.0]])]});}
            var Q208;
            {var subQ0=sQuery(id+"F0.wireOp",EDGE,"E238.MirrorCS");Q208=makeQuery(id+"F0.imprint","IMPRINT",FACE,{"disambiguationData":[TD([[makeQuery(id+"F0.imprint","IMPRINT",EDGE,{"derivedFrom":subQ0}),-1.0]])]});}
            var Q209;
            {var subQ3=sQuery(id+"F0.wireOp",EDGE,"E236.MirrorCS");Q209=makeQuery(id+"F0.imprint","IMPRINT",FACE,{"disambiguationData":[TD([[makeQuery(id+"F0.imprint","IMPRINT",EDGE,{"derivedFrom":subQ3}),-1.0]])]});}
            var Q210;
            {var subQ0=sQuery(id+"F0.wireOp",EDGE,"E237.MirrorCS");Q210=makeQuery(id+"F0.imprint","IMPRINT",FACE,{"disambiguationData":[TD([[makeQuery(id+"F0.imprint","IMPRINT",EDGE,{"derivedFrom":subQ0}),-1.0]])]});}
            var Q211;
            {var subQ3=sQuery(id+"F0.wireOp",EDGE,"E245.MirrorCS");Q211=makeQuery(id+"F0.imprint","IMPRINT",FACE,{"disambiguationData":[TD([[makeQuery(id+"F0.imprint","IMPRINT",EDGE,{"derivedFrom":subQ3}),1.0]])]});}
            var Q212;
            {var subQ3=sQuery(id+"F0.wireOp",EDGE,"E246.MirrorCS");Q212=makeQuery(id+"F0.imprint","IMPRINT",FACE,{"disambiguationData":[TD([[makeQuery(id+"F0.imprint","IMPRINT",EDGE,{"derivedFrom":subQ3}),1.0]])]});}
            var Q213;
            {var subQ3=sQuery(id+"F0.wireOp",EDGE,"E247.MirrorCS");Q213=makeQuery(id+"F0.imprint","IMPRINT",FACE,{"disambiguationData":[TD([[makeQuery(id+"F0.imprint","IMPRINT",EDGE,{"derivedFrom":subQ3}),1.0]])]});}
            var Q214;
            {var subQ3=sQuery(id+"F0.wireOp",EDGE,"E243.MirrorCS");Q214=makeQuery(id+"F0.imprint","IMPRINT",FACE,{"disambiguationData":[TD([[makeQuery(id+"F0.imprint","IMPRINT",EDGE,{"derivedFrom":subQ3}),1.0]])]});}
            var Q215;
            {var subQ3=sQuery(id+"F0.wireOp",EDGE,"E241.MirrorCS");Q215=makeQuery(id+"F0.imprint","IMPRINT",FACE,{"disambiguationData":[TD([[makeQuery(id+"F0.imprint","IMPRINT",EDGE,{"derivedFrom":subQ3}),1.0]])]});}
            var Q216;
            {var subQ0=sQuery(id+"F0.wireOp",EDGE,"E158.MirrorCS");Q216=makeQuery(id+"F0.imprint","IMPRINT",FACE,{"disambiguationData":[TD([[makeQuery(id+"F0.imprint","IMPRINT",EDGE,{"derivedFrom":subQ0}),1.0]])]});}
            var Q217;
            {var subQ3=sQuery(id+"F0.wireOp",EDGE,"E157.MirrorCS");Q217=makeQuery(id+"F0.imprint","IMPRINT",FACE,{"disambiguationData":[TD([[makeQuery(id+"F0.imprint","IMPRINT",EDGE,{"derivedFrom":subQ3}),1.0]])]});}
            var Q218;
            {var subQ0=sQuery(id+"F0.wireOp",EDGE,"E159.MirrorCS");Q218=makeQuery(id+"F0.imprint","IMPRINT",FACE,{"disambiguationData":[TD([[makeQuery(id+"F0.imprint","IMPRINT",EDGE,{"derivedFrom":subQ0}),1.0]])]});}
            var Q219;
            {var subQ0=sQuery(id+"F0.wireOp",EDGE,"E171.MirrorCS");Q219=makeQuery(id+"F0.imprint","IMPRINT",FACE,{"disambiguationData":[TD([[makeQuery(id+"F0.imprint","IMPRINT",EDGE,{"derivedFrom":subQ0}),1.0]])]});}
            var Q220;
            {var subQ3=sQuery(id+"F0.wireOp",EDGE,"E172.MirrorCS");Q220=makeQuery(id+"F0.imprint","IMPRINT",FACE,{"disambiguationData":[TD([[makeQuery(id+"F0.imprint","IMPRINT",EDGE,{"derivedFrom":subQ3}),1.0]])]});}
            var Q221;
            {var subQ0=sQuery(id+"F0.wireOp",EDGE,"E170.MirrorCS");Q221=makeQuery(id+"F0.imprint","IMPRINT",FACE,{"disambiguationData":[TD([[makeQuery(id+"F0.imprint","IMPRINT",EDGE,{"derivedFrom":subQ0}),1.0]])]});}
            var Q222;
            {var subQ0=sQuery(id+"F0.wireOp",EDGE,"E169.MirrorCS");Q222=makeQuery(id+"F0.imprint","IMPRINT",FACE,{"disambiguationData":[TD([[makeQuery(id+"F0.imprint","IMPRINT",EDGE,{"derivedFrom":subQ0}),1.0]])]});}
            var Q223;
            {var subQ0=sQuery(id+"F0.wireOp",EDGE,"E167.MirrorCS");Q223=makeQuery(id+"F0.imprint","IMPRINT",FACE,{"disambiguationData":[TD([[makeQuery(id+"F0.imprint","IMPRINT",EDGE,{"derivedFrom":subQ0}),1.0]])]});}
            var Q224;
            {var subQ3=sQuery(id+"F0.wireOp",EDGE,"E168.MirrorCS");Q224=makeQuery(id+"F0.imprint","IMPRINT",FACE,{"disambiguationData":[TD([[makeQuery(id+"F0.imprint","IMPRINT",EDGE,{"derivedFrom":subQ3}),1.0]])]});}
            var Q225;
            {var subQ3=sQuery(id+"F0.wireOp",EDGE,"E164.MirrorCS");Q225=makeQuery(id+"F0.imprint","IMPRINT",FACE,{"disambiguationData":[TD([[makeQuery(id+"F0.imprint","IMPRINT",EDGE,{"derivedFrom":subQ3}),1.0]])]});}
            var Q226;
            {var subQ3=sQuery(id+"F0.wireOp",EDGE,"E166.MirrorCS");Q226=makeQuery(id+"F0.imprint","IMPRINT",FACE,{"disambiguationData":[TD([[makeQuery(id+"F0.imprint","IMPRINT",EDGE,{"derivedFrom":subQ3}),1.0]])]});}
            var Q227;
            {var subQ3=sQuery(id+"F0.wireOp",EDGE,"E165.MirrorCS");Q227=makeQuery(id+"F0.imprint","IMPRINT",FACE,{"disambiguationData":[TD([[makeQuery(id+"F0.imprint","IMPRINT",EDGE,{"derivedFrom":subQ3}),1.0]])]});}
            var Q228;
            {var subQ3=sQuery(id+"F0.wireOp",EDGE,"E161.MirrorCS");Q228=makeQuery(id+"F0.imprint","IMPRINT",FACE,{"disambiguationData":[TD([[makeQuery(id+"F0.imprint","IMPRINT",EDGE,{"derivedFrom":subQ3}),-1.0]])]});}
            var Q229;
            {var subQ3=sQuery(id+"F0.wireOp",EDGE,"E162.MirrorCS");Q229=makeQuery(id+"F0.imprint","IMPRINT",FACE,{"disambiguationData":[TD([[makeQuery(id+"F0.imprint","IMPRINT",EDGE,{"derivedFrom":subQ3}),-1.0]])]});}
            var Q230;
            {var subQ3=sQuery(id+"F0.wireOp",EDGE,"E163.MirrorCS");Q230=makeQuery(id+"F0.imprint","IMPRINT",FACE,{"disambiguationData":[TD([[makeQuery(id+"F0.imprint","IMPRINT",EDGE,{"derivedFrom":subQ3}),-1.0]])]});}
            var Q231;
            {var subQ0=sQuery(id+"F0.wireOp",EDGE,"E154.MirrorCS");Q231=makeQuery(id+"F0.imprint","IMPRINT",FACE,{"disambiguationData":[TD([[makeQuery(id+"F0.imprint","IMPRINT",EDGE,{"derivedFrom":subQ0}),-1.0]])]});}
            var Q232;
            {var subQ0=sQuery(id+"F0.wireOp",EDGE,"E153.MirrorCS");Q232=makeQuery(id+"F0.imprint","IMPRINT",FACE,{"disambiguationData":[TD([[makeQuery(id+"F0.imprint","IMPRINT",EDGE,{"derivedFrom":subQ0}),-1.0]])]});}
            var Q233;
            {var subQ3=sQuery(id+"F0.wireOp",EDGE,"E152.MirrorCS");Q233=makeQuery(id+"F0.imprint","IMPRINT",FACE,{"disambiguationData":[TD([[makeQuery(id+"F0.imprint","IMPRINT",EDGE,{"derivedFrom":subQ3}),-1.0]])]});}
            var Q234;
            {var subQ3=sQuery(id+"F0.wireOp",EDGE,"E187.MirrorCS");Q234=makeQuery(id+"F0.imprint","IMPRINT",FACE,{"disambiguationData":[TD([[makeQuery(id+"F0.imprint","IMPRINT",EDGE,{"derivedFrom":subQ3}),1.0]])]});}
            var Q235;
            {var subQ3=sQuery(id+"F0.wireOp",EDGE,"E186.MirrorCS");Q235=makeQuery(id+"F0.imprint","IMPRINT",FACE,{"disambiguationData":[TD([[makeQuery(id+"F0.imprint","IMPRINT",EDGE,{"derivedFrom":subQ3}),1.0]])]});}
            var Q236;
            {var subQ3=sQuery(id+"F0.wireOp",EDGE,"E185.MirrorCS");Q236=makeQuery(id+"F0.imprint","IMPRINT",FACE,{"disambiguationData":[TD([[makeQuery(id+"F0.imprint","IMPRINT",EDGE,{"derivedFrom":subQ3}),1.0]])]});}
            var Q237;
            {var subQ3=sQuery(id+"F0.wireOp",EDGE,"E182.MirrorCS");Q237=makeQuery(id+"F0.imprint","IMPRINT",FACE,{"disambiguationData":[TD([[makeQuery(id+"F0.imprint","IMPRINT",EDGE,{"derivedFrom":subQ3}),1.0]])]});}
            var Q238;
            {var subQ3=sQuery(id+"F0.wireOp",EDGE,"E183.MirrorCS");Q238=makeQuery(id+"F0.imprint","IMPRINT",FACE,{"disambiguationData":[TD([[makeQuery(id+"F0.imprint","IMPRINT",EDGE,{"derivedFrom":subQ3}),1.0]])]});}
            var Q239;
            {var subQ3=sQuery(id+"F0.wireOp",EDGE,"E181.MirrorCS");Q239=makeQuery(id+"F0.imprint","IMPRINT",FACE,{"disambiguationData":[TD([[makeQuery(id+"F0.imprint","IMPRINT",EDGE,{"derivedFrom":subQ3}),1.0]])]});}
            var Q240;
            {var subQ0=sQuery(id+"F0.wireOp",EDGE,"E178.MirrorCS");Q240=makeQuery(id+"F0.imprint","IMPRINT",FACE,{"disambiguationData":[TD([[makeQuery(id+"F0.imprint","IMPRINT",EDGE,{"derivedFrom":subQ0}),-1.0]])]});}
            var Q241;
            {var subQ0=sQuery(id+"F0.wireOp",EDGE,"E177.MirrorCS");Q241=makeQuery(id+"F0.imprint","IMPRINT",FACE,{"disambiguationData":[TD([[makeQuery(id+"F0.imprint","IMPRINT",EDGE,{"derivedFrom":subQ0}),-1.0]])]});}
            var Q242;
            {var subQ3=sQuery(id+"F0.wireOp",EDGE,"E176.MirrorCS");Q242=makeQuery(id+"F0.imprint","IMPRINT",FACE,{"disambiguationData":[TD([[makeQuery(id+"F0.imprint","IMPRINT",EDGE,{"derivedFrom":subQ3}),-1.0]])]});}
            extrude(context, id + "F1", {"entities" : qUnion([Q0, Q1, Q2, Q3, Q4, Q5, Q6, Q7, Q8, Q9, Q10, Q11, Q12, Q13, Q14, Q15, Q16, Q17, Q18, Q19, Q20, Q21, Q22, Q23, Q24, Q25, Q26, Q27, Q28, Q29, Q30, Q31, Q32, Q33, Q34, Q35, Q36, Q37, Q38, Q39, Q40, Q41, Q42, Q43, Q44, Q45, Q46, Q47, Q48, Q49, Q50, Q51, Q52, Q53, Q54, Q55, Q56, Q57, Q58, Q59, Q60, Q61, Q62, Q63, Q64, Q65, Q66, Q67, Q68, Q69, Q70, Q71, Q72, Q73, Q74, Q75, Q76, Q77, Q78, Q79, Q80, Q81, Q82, Q83, Q84, Q85, Q86, Q87, Q88, Q89, Q90, Q91, Q92, Q93, Q94, Q95, Q96, Q97, Q98, Q99, Q100, Q101, Q102, Q103, Q104, Q105, Q106, Q107, Q108, Q109, Q110, Q111, Q112, Q113, Q114, Q115, Q116, Q117, Q118, Q119, Q120, Q121, Q122, Q123, Q124, Q125, Q126, Q127, Q128, Q129, Q130, Q131, Q132, Q133, Q134, Q135, Q136, Q137, Q138, Q139, Q140, Q141, Q142, Q143, Q144, Q145, Q146, Q147, Q148, Q149, Q150, Q151, Q152, Q153, Q154, Q155, Q156, Q157, Q158, Q159, Q160, Q161, Q162, Q163, Q164, Q165, Q166, Q167, Q168, Q169, Q170, Q171, Q172, Q173, Q174, Q175, Q176, Q177, Q178, Q179, Q180, Q181, Q182, Q183, Q184, Q185, Q186, Q187, Q188, Q189, Q190, Q191, Q192, Q193, Q194, Q195, Q196, Q197, Q198, Q199, Q200, Q201, Q202, Q203, Q204, Q205, Q206, Q207, Q208, Q209, Q210, Q211, Q212, Q213, Q214, Q215, Q216, Q217, Q218, Q219, Q220, Q221, Q222, Q223, Q224, Q225, Q226, Q227, Q228, Q229, Q230, Q231, Q232, Q233, Q234, Q235, Q236, Q237, Q238, Q239, Q240, Q241, Q242]), "depth" : 12.7 * mm, "offsetDistance" : 25.4 * mm});
        }
    });
